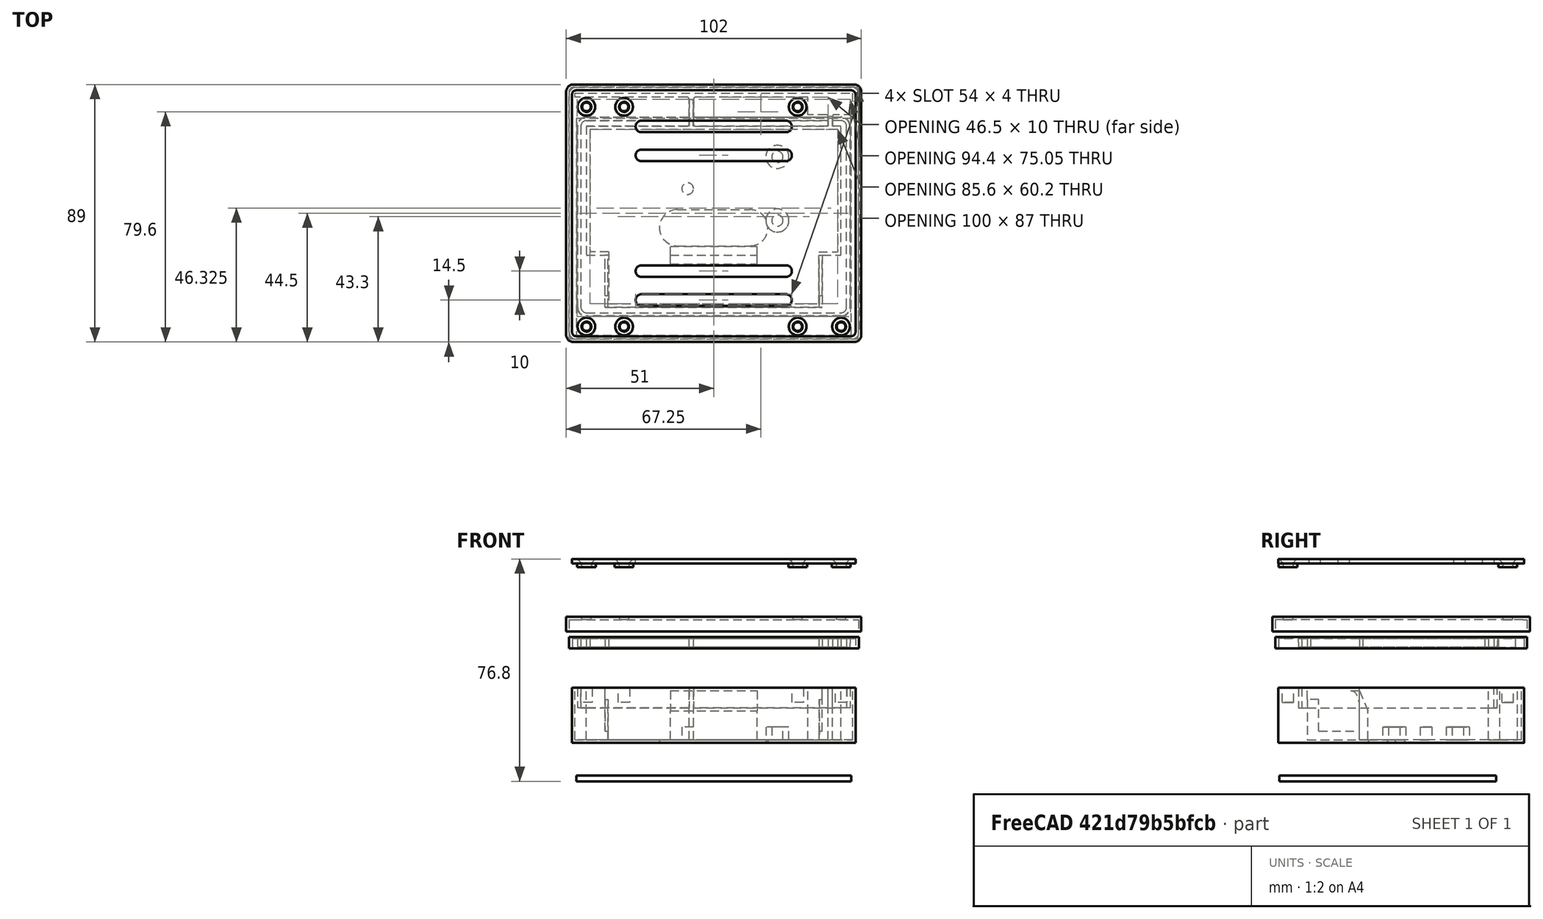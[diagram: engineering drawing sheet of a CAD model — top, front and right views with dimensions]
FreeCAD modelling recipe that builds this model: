
FCSTD DOCUMENT  (FreeCAD 1.1R20260325 (Git shallow))
Label: RAKTracker-v11.5
License: All rights reserved
objects: Sketcher::SketchObject×20, PartDesign::Pad×14, PartDesign::Body×5, App::Point×5, PartDesign::Pocket×4, PartDesign::SubShapeBinder×3, PartDesign::Plane×2, Spreadsheet::Sheet×1, PartDesign::AdditiveLoft×1, PartDesign::Hole×1
note: 110 computed .brp shape members not serialized (recipe doc carries the construction recipe); baked Part::Feature solids carry a one-line shape summary decoded from their .brp

FEATURE [Spreadsheet::Sheet] Spreadsheet  label="sheet"
  cells = A1='Components; D1='None-Component sizes; J1='TODO/NOTES; D3='M3 Insert Hole Dia; E3(InsetDiaM3)==3.9 mm; J3='We should really consider making the size of the panel the actual size and adjusting the boxantennaspace too.; A4='Solar Panel; D4='M2.5 Insert Hole DIa; E4(InsertDiaM2_5)==3.9 mm; J4='This means the panel needs to be aligned to one corner, and the antenna sizes need to create the width of the box.; A5='Panel width; B5(PanelWidth)==75 mm; D5='M3 Though Hall; E5(M3ThoughHoleDia)==3.2 mm; A6='Panel length; B6(PanelLength)==95 mm; D6='Insert Hole Depth; E6(InsertDepth)==8 mm; A7='Panel height; B7==1.5 mm; D8='PCB Mount Outer Diameter; E8(PCBMountDia)==8 mm; A9='Battery; D9='PCB Mount Height; E9(PCBMountHeight)==4.5 mm; A10='Battery Width; B10(BatteryWidth)==18 mm; D10='PCB Mount from Side; E10(PCBMountFromSide)==12 mm; A11='Battery Length; B11(BatteryLength)==65 mm; A12='Battery Height; B12(BatteryHeight)==18 mm; A13='Battery Mount Distance; B13(BatteryMountDistance)==75 mm; D14='Lid Wall Around sides; E14(LidWallAroundSides)==1 mm; A15='GPS Antenna Width; B15==15.5 mm; D15='Lid Wall Margin; E15==0.25 mm; A16='GPS Antenna Height; B16(AntGPSHeight)==7.5 mm; D16='Strap Mount Dia; E16(StrapMountDia)==8 mm; A17='GPS Antenna Length; B17(AntGPSLength)==15.5 mm; D17='Strap slot width; E17(StrapSlotWidth)==2 mm; D18='Strap slot distance; E18(StrapSlotDistance)==60 mm; A19='Small Molex Lora Antenna Width; B19(AntSmallLoraWidth)==10 mm; A20='Small Molex Lora Antenna Length; B20(AntSmallLoraLength)==80 mm; D20='SealWidth; E20(SealWidthTop)==1.2 mm; A21='Small Molex Lora Antenna Height; B21(AntSmallLoraHeight)==1.4 mm; D21='SealHeight; E21(SealHeight)==3 mm; D22='SealOuterWidth; E22(SealOuterWidth)==1 mm; A23='Large Molex Lora Antenna Width Sticker; B23(AntLargeLoraWidth)==12.5 mm; D23='Wall Width; E23(WallWidth)==5 mm; A24='Large Molex Lora Antenna Length Sticker; B24(AntLargeLoraLength)==87.5 mm; A25='Large Molex Lora Antenna Width (white); B25='TBD; A26='Large Molex Lora Antenna Length (white); B26==100 mm; D26='Bottom Thickness; E26(WallBottomThickness)==1 mm; A27='Large Molex Lora Antenna Height; B27(AntLargeLoraHeight)==1.6 mm; D27='Box Corner Radisu; E27(BoxCornerRadius)==1.5 mm; D28='BoxAntennaSpace; E28(BoxAntennaSpace)==10 mm; A29='Antenna Wire width; B29(AntWireWidth)==1.5 mm; A31='PCB Width; B31==30 mm; A32='PCB Length; B32==38 mm; A33='PCB Width With Margin; B33==31 mm; A34='PCB Length with Margin; B34==39 mm; A35='PCB Height; B35==16 mm; A36='PCB 2 Hole Distance; B36(PCBHoleDistance)==22 mm; A37='PCB Single Hole Distance from 2 Holes; B37(PCBHoleAwayFrom2Holes)==31 mm
FEATURE [Sketcher::SketchObject] Sketch  label="BoxBaseSketch"
  ArcFitTolerance = 1e-06
  AttachmentSupport = -> [XY_Plane]
  ExternalTypes = [0]
  FullyConstrained = true
  MakeInternals = false
  MapMode = 5
  _ExternalGeoVersion = 0
  expr: Constraints[18] = <<sheet>>.BoxCornerRadius
  expr: Constraints[28] = <<sheet>>.PanelLength
  expr: Constraints[29] = <<sheet>>.PanelWidth
  expr: Constraints[31] = <<sheet>>.BoxAntennaSpace
  expr: Constraints[40] = <<sheet>>.PanelWidth / 2
  sketch-geometry (18):
    g0: LineSegment StartX=-47.5 StartY=-42.5 StartZ=0 EndX=47.5 EndY=-42.5 EndZ=0
    g1: LineSegment StartX=49 StartY=-41 StartZ=0 EndX=49 EndY=41 EndZ=0
    g2: LineSegment StartX=47.5 StartY=42.5 StartZ=0 EndX=-47.5 EndY=42.5 EndZ=0
    g3: LineSegment StartX=-49 StartY=41 StartZ=0 EndX=-49 EndY=-41 EndZ=0
    g4: ArcOfCircle CenterX=-47.5 CenterY=-41 CenterZ=0 NormalX=0 NormalY=0 NormalZ=1 AngleXU=0 Radius=1.5 StartAngle=3.14159 EndAngle=4.71239
    g5: ArcOfCircle CenterX=47.5 CenterY=-41 CenterZ=0 NormalX=0 NormalY=0 NormalZ=1 AngleXU=0 Radius=1.5 StartAngle=4.71239 EndAngle=6.28319
    g6: ArcOfCircle CenterX=47.5 CenterY=41 CenterZ=0 NormalX=0 NormalY=0 NormalZ=1 AngleXU=0 Radius=1.5 StartAngle=-1.8e-15 EndAngle=1.5708
    g7: ArcOfCircle CenterX=-47.5 CenterY=41 CenterZ=0 NormalX=0 NormalY=0 NormalZ=1 AngleXU=0 Radius=1.5 StartAngle=1.5708 EndAngle=3.14159
    g8: GeomPoint [constr] X=49 Y=42.5 Z=0
    g9: GeomPoint [constr] X=0 Y=0 Z=0
    g10: LineSegment [constr] StartX=47.5 StartY=-42.5 StartZ=0 EndX=47.5 EndY=32.5 EndZ=0
    g11: LineSegment [constr] StartX=47.5 StartY=32.5 StartZ=0 EndX=-47.5 EndY=32.5 EndZ=0
    g12: LineSegment [constr] StartX=-47.5 StartY=32.5 StartZ=0 EndX=-47.5 EndY=-42.5 EndZ=0
    g13: LineSegment [constr] StartX=-47.5 StartY=-42.5 StartZ=0 EndX=47.5 EndY=-42.5 EndZ=0
    g14: ArcOfCircle CenterX=-12.5 CenterY=-5 CenterZ=0 NormalX=0 NormalY=0 NormalZ=1 AngleXU=0 Radius=6.25 StartAngle=1.5708 EndAngle=4.71239
    g15: ArcOfCircle CenterX=12.5 CenterY=-5 CenterZ=0 NormalX=0 NormalY=0 NormalZ=1 AngleXU=0 Radius=6.25 StartAngle=4.71239 EndAngle=7.85398
    g16: LineSegment StartX=-12.5 StartY=1.25 StartZ=0 EndX=12.5 EndY=1.25 EndZ=0
    g17: LineSegment StartX=-12.5 StartY=-11.25 StartZ=0 EndX=12.5 EndY=-11.25 EndZ=0
  constraints (41):
    c: Tangent(g0,g4) = -1.5708
    c: Tangent(g0,g5) = -1.5708
    c: Tangent(g1,g5) = -1.5708
    c: Tangent(g1,g6) = -1.5708
    c: Tangent(g2,g6) = -1.5708
    c: Tangent(g2,g7) = -1.5708
    c: Tangent(g3,g7) = -1.5708
    c: Tangent(g3,g4) = -1.5708
    c: Horizontal(g0)
    c: Horizontal(g2)
    c: Vertical(g1)
    c: Vertical(g3)
    c: Equal(g4,g5)
    c: Equal(g5,g6)
    c: Equal(g6,g7)
    c: Symmetric(g2,g0,g9)
    c: PointOnObject(g8,g1)
    c: PointOnObject(g8,g2)
    c: Radius(g5) = 1.5
    c: Coincident(g9,g-1)
    c: Coincident(g10,g11)
    c: Coincident(g11,g12)
    c: Coincident(g12,g13)
    c: Coincident(g13,g10)
    c: Vertical(g10)
    c: Vertical(g12)
    c: Horizontal(g11)
    c: Coincident(g10,g0)
    c: DistanceX(g12,g0) = 95
    c: DistanceY(g10,g10) = 75
    c: Coincident(g12,g0)
    c: DistanceY(g10,g2) = 10
    c: Tangent(g14,g16) = 1.5708
    c: Tangent(g14,g17) = -1.5708
    c: Tangent(g15,g16) = 1.5708
    c: Tangent(g15,g17) = -1.5708
    c: Equal(g14,g15)
    c: Distance(g15,g15) = 12.5
    c: DistanceX(g14,g15) = 25
    c: Symmetric(g14,g15,g-2)
    c: DistanceY(g15,g10) = 37.5
FEATURE [PartDesign::Pad] Pad  label="BoxBase"
  Direction = (0,0,1)
  Length = 1
  Length2 = 10
  Profile = -> Sketch
  ReferenceAxis = -> Sketch [N_Axis]
  SideType = 0
  Suppressed = false
  Type = 0
  Type2 = 0
  expr: Length = <<sheet>>.WallBottomThickness
FEATURE [Sketcher::SketchObject] Sketch001  label="BoxOuterWallSketch"
  ArcFitTolerance = 1e-06
  AttachmentSupport = -> [XY_Plane]
  ExternalTypes = [0]
  FullyConstrained = true
  MakeInternals = false
  MapMode = 5
  _ExternalGeoVersion = 0
  expr: Constraints[100] = <<sheet>>.PanelWidth
  expr: Constraints[101] = <<sheet>>.PanelLength
  expr: Constraints[103] = <<sheet>>.BoxAntennaSpace
  expr: Constraints[115] = <<sheet>>.BoxCornerRadius
  expr: Constraints[129] = <<sheet>>.WallWidth
  expr: Constraints[49] = <<sheet>>.AntGPSLength
  expr: Constraints[50] = <<sheet>>.AntWireWidth
  expr: Constraints[51] = <<sheet>>.BatteryMountDistance
  expr: Constraints[52] = <<sheet>>.WallWidth * 2
  expr: Constraints[53] = <<sheet>>.WallWidth
  expr: Constraints[54] = <<sheet>>.BatteryWidth
  expr: Constraints[87] = <<sheet>>.AntWireWidth
  expr: Constraints[90] = <<sheet>>.AntSmallLoraHeight
  expr: Constraints[91] = <<sheet>>.AntGPSHeight
  expr: Constraints[92] = <<sheet>>.WallWidth * 2
  sketch-geometry (48):
    g0: LineSegment StartX=-47.5 StartY=-42.5 StartZ=0 EndX=47.5 EndY=-42.5 EndZ=0
    g1: LineSegment StartX=49 StartY=-41 StartZ=0 EndX=49 EndY=41 EndZ=0
    g2: LineSegment StartX=47.5 StartY=42.5 StartZ=0 EndX=-47.5 EndY=42.5 EndZ=0
    g3: LineSegment StartX=44 StartY=30.1 StartZ=0 EndX=44 EndY=-14.5 EndZ=0
    g4: LineSegment StartX=44 StartY=-14.5 StartZ=0 EndX=37.5 EndY=-14.5 EndZ=0
    g5: LineSegment StartX=37.5 StartY=-14.5 StartZ=0 EndX=37.5 EndY=-32.5 EndZ=0
    g6: LineSegment StartX=37.5 StartY=-32.5 StartZ=0 EndX=-37.5 EndY=-32.5 EndZ=0
    g7: LineSegment StartX=-37.5 StartY=-32.5 StartZ=0 EndX=-37.5 EndY=-14.5 EndZ=0
    g8: LineSegment StartX=-37.5 StartY=-14.5 StartZ=0 EndX=-44 EndY=-14.5 EndZ=0
    g9: LineSegment StartX=-44 StartY=-14.5 StartZ=0 EndX=-44 EndY=30.1 EndZ=0
    g10: LineSegment StartX=-44 StartY=30.1 StartZ=0 EndX=-9.25 EndY=30.1 EndZ=0
    g11: LineSegment StartX=-8.5 StartY=30.85 StartZ=0 EndX=-8.5 EndY=39.35 EndZ=0
    g12: LineSegment StartX=-9.25 StartY=40.1 StartZ=0 EndX=-48 EndY=40.1 EndZ=0
    g13: LineSegment StartX=-48 StartY=40.1 StartZ=0 EndX=-48 EndY=41.5 EndZ=0
    g14: LineSegment StartX=-48 StartY=41.5 StartZ=0 EndX=48 EndY=41.5 EndZ=0
    g15: LineSegment StartX=-7 StartY=30.85 StartZ=0 EndX=-7 EndY=39.35 EndZ=0
    g16: LineSegment StartX=-6.25 StartY=40.1 StartZ=0 EndX=32.5 EndY=40.1 EndZ=0
    g17: LineSegment StartX=32.5 StartY=40.1 StartZ=0 EndX=32.5 EndY=34 EndZ=0
    g18: LineSegment StartX=48 StartY=34 StartZ=0 EndX=48 EndY=41.5 EndZ=0
    g19: ArcOfCircle CenterX=-9.25 CenterY=39.35 CenterZ=0 NormalX=0 NormalY=0 NormalZ=1 AngleXU=0 Radius=0.75 StartAngle=3e-15 EndAngle=1.5708
    g20: GeomPoint [constr] X=-8.5 Y=40.1 Z=0
    g21: ArcOfCircle CenterX=-6.25 CenterY=39.35 CenterZ=0 NormalX=0 NormalY=0 NormalZ=1 AngleXU=0 Radius=0.75 StartAngle=1.5708 EndAngle=3.14159
    g22: ArcOfCircle CenterX=-9.25 CenterY=30.85 CenterZ=0 NormalX=0 NormalY=0 NormalZ=1 AngleXU=0 Radius=0.75 StartAngle=4.71239 EndAngle=6.28319
    g23: GeomPoint [constr] X=-8.5 Y=30.1 Z=0
    g24: ArcOfCircle CenterX=-6.25 CenterY=30.85 CenterZ=0 NormalX=0 NormalY=0 NormalZ=1 AngleXU=0 Radius=0.75 StartAngle=3.14159 EndAngle=4.71239
    g25: LineSegment StartX=32.5 StartY=34 StartZ=0 EndX=39 EndY=34 EndZ=0
    g26: LineSegment StartX=39.5 StartY=33.5 StartZ=0 EndX=39.5 EndY=30.6 EndZ=0
    g27: LineSegment StartX=39 StartY=30.1 StartZ=0 EndX=-6.25 EndY=30.1 EndZ=0
    g28: LineSegment StartX=48 StartY=34 StartZ=0 EndX=41.5 EndY=34 EndZ=0
    g29: LineSegment StartX=41 StartY=33.5 StartZ=0 EndX=41 EndY=30.6 EndZ=0
    g30: LineSegment StartX=41.5 StartY=30.1 StartZ=0 EndX=44 EndY=30.1 EndZ=0
    g31: ArcOfCircle CenterX=39 CenterY=33.5 CenterZ=0 NormalX=0 NormalY=0 NormalZ=1 AngleXU=0 Radius=0.5 StartAngle=0 EndAngle=1.5708
    g32: GeomPoint [constr] X=39.5 Y=34 Z=0
    g33: ArcOfCircle CenterX=41.5 CenterY=33.5 CenterZ=0 NormalX=0 NormalY=0 NormalZ=1 AngleXU=0 Radius=0.5 StartAngle=1.5708 EndAngle=3.14159
    g34: GeomPoint [constr] X=41 Y=34 Z=0
    g35: ArcOfCircle CenterX=39 CenterY=30.6 CenterZ=0 NormalX=0 NormalY=0 NormalZ=1 AngleXU=0 Radius=0.5 StartAngle=4.71239 EndAngle=6.28319
    g36: GeomPoint [constr] X=39.5 Y=30.1 Z=0
    g37: ArcOfCircle CenterX=41.5 CenterY=30.6 CenterZ=0 NormalX=0 NormalY=0 NormalZ=1 AngleXU=0 Radius=0.5 StartAngle=3.14159 EndAngle=4.71239
    g38: GeomPoint [constr] X=41 Y=30.1 Z=0
    g39: LineSegment [constr] StartX=-47.5 StartY=32.5 StartZ=0 EndX=-47.5 EndY=-42.5 EndZ=0
    g40: LineSegment [constr] StartX=-47.5 StartY=-42.5 StartZ=0 EndX=47.5 EndY=-42.5 EndZ=0
    g41: LineSegment [constr] StartX=47.5 StartY=-42.5 StartZ=0 EndX=47.5 EndY=32.5 EndZ=0
    g42: LineSegment [constr] StartX=47.5 StartY=32.5 StartZ=0 EndX=-47.5 EndY=32.5 EndZ=0
    g43: LineSegment StartX=-49 StartY=41 StartZ=0 EndX=-49 EndY=-41 EndZ=0
    g44: ArcOfCircle CenterX=-47.5 CenterY=-41 CenterZ=0 NormalX=0 NormalY=0 NormalZ=1 AngleXU=0 Radius=1.5 StartAngle=3.14159 EndAngle=4.71239
    g45: ArcOfCircle CenterX=47.5 CenterY=-41 CenterZ=0 NormalX=0 NormalY=0 NormalZ=1 AngleXU=0 Radius=1.5 StartAngle=4.71239 EndAngle=6.28319
    g46: ArcOfCircle CenterX=47.5 CenterY=41 CenterZ=0 NormalX=0 NormalY=0 NormalZ=1 AngleXU=0 Radius=1.5 StartAngle=0 EndAngle=1.5708
    g47: ArcOfCircle CenterX=-47.5 CenterY=41 CenterZ=0 NormalX=0 NormalY=0 NormalZ=1 AngleXU=0 Radius=1.5 StartAngle=1.5708 EndAngle=3.14159
  constraints (132):
    c: Vertical(g1)
    c: Horizontal(g2)
    c: Vertical(g3)
    c: Coincident(g3,g4)
    c: Horizontal(g4)
    c: Coincident(g4,g5)
    c: Vertical(g5)
    c: Coincident(g5,g6)
    c: Horizontal(g6)
    c: Coincident(g6,g7)
    c: Vertical(g7)
    c: Coincident(g7,g8)
    c: Coincident(g8,g9)
    c: Vertical(g9)
    c: Coincident(g9,g10)
    c: Horizontal(g10)
    c: Coincident(g12,g13)
    c: Coincident(g13,g14)
    c: Horizontal(g14)
    c: Horizontal(g8)
    c: Vertical(g15)
    c: Horizontal(g16)
    c: Coincident(g16,g17)
    c: Coincident(g18,g14)
    c: Vertical(g18)
    c: Vertical(g17)
    c: Vertical(g11)
    c: Vertical(g13)
    c: Horizontal(g12)
    c: PointOnObject(g20,g12)
    c: PointOnObject(g20,g11)
    c: Tangent(g12,g19) = -1.5708
    c: Tangent(g11,g19) = -1.5708
    c: Tangent(g15,g21) = 1.5708
    c: Tangent(g16,g21) = 1.5708
    c: PointOnObject(g23,g11)
    c: PointOnObject(g23,g10)
    c: Tangent(g11,g22) = -1.5708
    c: Tangent(g10,g22) = -1.5708
    c: Tangent(g15,g24) = 1.5708
    c: Radius(g19) = 0.75
    c: Equal(g19,g22)
    c: Equal(g22,g21)
    c: Equal(g21,g24)
    c: Horizontal(g11,g15)
    c: Horizontal(g7,g4)
    c: Equal(g8,g4)
    c: DistanceY(g13,g2) = 1
    c: DistanceX(g14,g1) = 1
    c: DistanceX(g17,g18) = 15.5
    c: DistanceX(g11,g15) = 1.5
    c: DistanceX(g7,g4) = 75
    c: DistanceY(g0,g6) = 10
    c: DistanceX(g3,g1) = 5
    c: DistanceY(g5,g4) = 18
    c: Coincident(g17,g25)
    c: Coincident(g27,g24)
    c: Horizontal(g27)
    c: Coincident(g18,g28)
    c: Horizontal(g28)
    c: Coincident(g30,g3)
    c: Horizontal(g25)
    c: Vertical(g29)
    c: Vertical(g26)
    c: Horizontal(g30)
    c: PointOnObject(g32,g25)
    c: PointOnObject(g32,g26)
    c: Tangent(g25,g31) = 1.5708
    c: Tangent(g26,g31) = 1.5708
    c: PointOnObject(g34,g29)
    c: PointOnObject(g34,g28)
    c: Tangent(g29,g33) = -1.5708
    c: Tangent(g28,g33) = -1.5708
    c: PointOnObject(g36,g26)
    c: PointOnObject(g36,g27)
    c: Tangent(g26,g35) = 1.5708
    c: Tangent(g27,g35) = 1.5708
    c: PointOnObject(g38,g30)
    c: PointOnObject(g38,g29)
    c: Tangent(g30,g37) = -1.5708
    c: Tangent(g29,g37) = -1.5708
    c: Radius(g31) = 0.5
    c: Equal(g31,g33)
    c: Equal(g33,g35)
    c: Equal(g35,g37)
    c: Horizontal(g30,g27)
    c: Horizontal(g25,g28)
    c: DistanceX(g26,g29) = 1.5
    c: Equal(g25,g28)
    c: Horizontal(g10,g24)
    c: DistanceY(g12,g13) = 1.4
    c: DistanceY(g18,g14) = 7.5
    c: DistanceY(g9,g12) = 10
    c: Coincident(g39,g40)
    c: Coincident(g41,g42)
    c: Coincident(g42,g39)
    c: Vertical(g39)
    c: Vertical(g41)
    c: Horizontal(g42)
    c: Horizontal(g0)
    c: DistanceY(g39,g39) = 75
    c: DistanceX(g40,g40) = 95
    c: Coincident(g41,g40)
    c: DistanceY(g41,g2) = 10
    c: Coincident(g0,g39)
    c: Coincident(g0,g40)
    c: Vertical(g43)
    c: Coincident(g44,g0)
    c: Coincident(g44,g43)
    c: Coincident(g45,g0)
    c: Coincident(g45,g1)
    c: Coincident(g46,g2)
    c: Coincident(g46,g1)
    c: Coincident(g47,g43)
    c: Coincident(g47,g2)
    c: Radius(g47) = 1.5
    c: Horizontal(g47,g43)
    c: Vertical(g47,g2)
    c: Equal(g47,g46)
    c: Vertical(g2,g46)
    c: Horizontal(g1,g46)
    c: Vertical(g44,g0)
    c: Horizontal(g43,g44)
    c: Horizontal(g1,g45)
    c: Vertical(g0,g45)
    c: DistanceX(g43,g12) = 1
    c: Symmetric(g2,g0,g-1)
    c: Vertical(g39,g47)
    c: Vertical(g41,g46)
    c: DistanceX(g43,g8) = 5
    c: DistanceX(g12,g11) = 39.5
    c: Horizontal(g12,g16)
FEATURE [PartDesign::Pad] Pad001  label="BoxWall"
  BaseFeature = -> Pad
  Direction = (0,0,1)
  Length = 19
  Length2 = 10
  Profile = -> Sketch001
  ReferenceAxis = -> Sketch001 [N_Axis]
  SideType = 0
  Suppressed = false
  Type = 0
  Type2 = 0
  expr: Length = <<sheet>>.BatteryWidth + <<sheet>>.WallBottomThickness
FEATURE [Sketcher::SketchObject] Sketch002  label="BoxPCBMountSketch"
  ArcFitTolerance = 1e-06
  AttachmentSupport = -> [XY_Plane]
  ExternalGeometry = -> [Sketch001]
  ExternalTypes = [0]
  FullyConstrained = true
  MakeInternals = false
  MapMode = 5
  _ExternalGeoVersion = 0
  expr: Constraints[10] = <<sheet>>.PCBMountFromSide
  expr: Constraints[11] = <<sheet>>.PCBHoleAwayFrom2Holes
  expr: Constraints[2] = <<sheet>>.InsetDiaM3
  expr: Constraints[5] = <<sheet>>.PCBMountDia
  expr: Constraints[7] = <<sheet>>.PCBHoleDistance
  expr: Constraints[8] = <<sheet>>.PCBMountDia / 2
  expr: Constraints[9] = <<sheet>>.PCBHoleDistance / 2
  sketch-geometry (5):
    g0: Circle CenterX=22 CenterY=19.5 CenterZ=0 NormalX=0 NormalY=0 NormalZ=1 AngleXU=0 Radius=4
    g1: Circle CenterX=22 CenterY=-2.5 CenterZ=0 NormalX=0 NormalY=0 NormalZ=1 AngleXU=0 Radius=4
    g2: Circle CenterX=22 CenterY=-2.5 CenterZ=0 NormalX=0 NormalY=0 NormalZ=1 AngleXU=0 Radius=1.95
    g3: Circle CenterX=22 CenterY=19.5 CenterZ=0 NormalX=0 NormalY=0 NormalZ=1 AngleXU=0 Radius=1.95
    g4: Circle CenterX=-9 CenterY=8.5 CenterZ=0 NormalX=0 NormalY=0 NormalZ=1 AngleXU=0 Radius=2
  constraints (13):
    c: Coincident(g2,g1)
    c: Coincident(g3,g0)
    c: Diameter(g3) = 3.9
    c: Equal(g3,g2)
    c: Vertical(g1,g0)
    c: Diameter(g0) = 8
    c: Equal(g0,g1)
    c: DistanceY(g1,g0) = 22
    c: Diameter(g4) = 4
    c: DistanceY(g1,g4) = 11
    c: DistanceY(g-3,g1) = 12
    c: DistanceX(g4,g0) = 31
    c: DistanceX(g1,g-3) = 22
FEATURE [PartDesign::Pad] Pad002  label="BoxPCBMount"
  BaseFeature = -> Pad001
  Direction = (0,0,1)
  Length = 5.5
  Length2 = 10
  Profile = -> Sketch002
  ReferenceAxis = -> Sketch002 [N_Axis]
  SideType = 0
  Suppressed = false
  Type = 0
  Type2 = 0
  expr: Length = <<sheet>>.WallBottomThickness + <<sheet>>.PCBMountHeight
FEATURE [Sketcher::SketchObject] Sketch003  label="BoxBatteryHolderSketch"
  ArcFitTolerance = 1e-06
  AttachmentSupport = -> [YZ_Plane]
  ExternalGeometry = -> [Sketch001]
  ExternalTypes = [0]
  FullyConstrained = true
  MakeInternals = false
  MapMode = 5
  Placement = pos=(0,0,0) rot=(0.57735,0.57735,0.57735;2.0944rad)
  _ExternalGeoVersion = 0
  expr: Constraints[21] = <<sheet>>.BatteryWidth
  sketch-geometry (11):
    g0: LineSegment StartX=-14.5 StartY=0 StartZ=0 EndX=-14.5 EndY=11 EndZ=0
    g1: LineSegment StartX=-14.5 StartY=0 StartZ=0 EndX=-11.5 EndY=0 EndZ=0
    g2: LineSegment StartX=-11.5 StartY=0 StartZ=0 EndX=-11.5 EndY=11 EndZ=0
    g3: Circle [constr] CenterX=-17.5 CenterY=18 CenterZ=0 NormalX=0 NormalY=0 NormalZ=1 AngleXU=0 Radius=1
    g4: Circle [constr] CenterX=-14.5 CenterY=18 CenterZ=0 NormalX=0 NormalY=0 NormalZ=1 AngleXU=0 Radius=1
    g5: Circle [constr] CenterX=-14.5 CenterY=11 CenterZ=0 NormalX=0 NormalY=0 NormalZ=1 AngleXU=0 Radius=1
    g6: BSplineCurve PolesCount=3 KnotsCount=2 Degree=2 IsPeriodic=0
    g7: GeomPoint [constr] X=-17.5 Y=18 Z=0
    g8: GeomPoint [constr] X=-14.5 Y=11 Z=0
    g9: LineSegment StartX=-17.5 StartY=18 StartZ=0 EndX=-14.5 EndY=18 EndZ=0
    g10: LineSegment StartX=-14.5 StartY=18 StartZ=0 EndX=-11.5 EndY=11 EndZ=0
  constraints (26):
    c: Coincident(g0,g-3)
    c: Vertical(g0)
    c: Coincident(g1,g0)
    c: PointOnObject(g1,g-1)
    c: Coincident(g2,g1)
    c: Vertical(g2)
    c: Weight(g3) = 1
    c: Equal(g3,g4)
    c: Equal(g3,g5)
    c: InternalAlignment(g3,g6)
    c: InternalAlignment(g4,g6)
    c: InternalAlignment(g5,g6)
    c: InternalAlignment(g7,g6)
    c: InternalAlignment(g8,g6)
    c: Coincident(g6,g0)
    c: DistanceX(g1,g1) = 3
    c: DistanceY(g0,g0) = 11
    c: Coincident(g9,g6)
    c: Horizontal(g9)
    c: Coincident(g10,g9)
    c: Coincident(g10,g2)
    c: DistanceY(g1,g9) = 18
    c: Horizontal(g0,g2)
    c: DistanceX(g6,g9) = 3
    c: Vertical(g0,g9)
    c: Coincident(g4,g9)
FEATURE [PartDesign::Pad] Pad003  label="BoxBatteryHolder"
  BaseFeature = -> Pad002
  Direction = (1,0,0)
  Length = 30
  Length2 = 10
  Profile = -> Sketch003
  ReferenceAxis = -> Sketch003 [N_Axis]
  SideType = 2
  Suppressed = false
  Type = 0
  Type2 = 0
FEATURE [Sketcher::SketchObject] Sketch004  label="BoxSealPocketSketch"
  ArcFitTolerance = 1e-06
  AttachmentSupport = -> [Pad003]
  ExternalGeometry = -> [Sketch001]
  ExternalTypes = [0]
  FullyConstrained = true
  MakeInternals = false
  MapMode = 5
  Placement = pos=(0,0,19) rot=(0,0,1;0rad)
  _ExternalGeoVersion = 0
  expr: Constraints[33] = <<sheet>>.SealWidthTop
  expr: Constraints[34] = (<<sheet>>.WallWidth - <<sheet>>.SealWidthTop) / 2
  expr: Constraints[35] = (<<sheet>>.WallWidth - <<sheet>>.SealWidthTop) / 2
  expr: Constraints[38] = (<<sheet>>.WallWidth - <<sheet>>.SealWidthTop) / 2
  sketch-geometry (18):
    g0: LineSegment StartX=47.1 StartY=-32.5 StartZ=0 EndX=47.1 EndY=30.1 EndZ=0
    g1: LineSegment StartX=44 StartY=33.2 StartZ=0 EndX=-44 EndY=33.2 EndZ=0
    g2: LineSegment StartX=-47.1 StartY=30.1 StartZ=0 EndX=-47.1 EndY=-32.5 EndZ=0
    g3: LineSegment StartX=-44 StartY=-35.6 StartZ=0 EndX=44 EndY=-35.6 EndZ=0
    g4: ArcOfCircle CenterX=44 CenterY=-32.5 CenterZ=0 NormalX=0 NormalY=0 NormalZ=1 AngleXU=0 Radius=3.1 StartAngle=4.71239 EndAngle=6.28319
    g5: ArcOfCircle CenterX=44 CenterY=30.1 CenterZ=0 NormalX=0 NormalY=0 NormalZ=1 AngleXU=0 Radius=3.1 StartAngle=-5.33e-14 EndAngle=1.5708
    g6: ArcOfCircle CenterX=-44 CenterY=30.1 CenterZ=0 NormalX=0 NormalY=0 NormalZ=1 AngleXU=0 Radius=3.1 StartAngle=1.5708 EndAngle=3.14159
    g7: ArcOfCircle CenterX=-44 CenterY=-32.5 CenterZ=0 NormalX=0 NormalY=0 NormalZ=1 AngleXU=0 Radius=3.1 StartAngle=3.14159 EndAngle=4.71239
    g8: LineSegment StartX=45.9 StartY=-32.5 StartZ=0 EndX=45.9 EndY=30.1 EndZ=0
    g9: LineSegment StartX=44 StartY=32 StartZ=0 EndX=-44 EndY=32 EndZ=0
    g10: LineSegment StartX=-45.9 StartY=30.1 StartZ=0 EndX=-45.9 EndY=-32.5 EndZ=0
    g11: LineSegment StartX=-44 StartY=-34.4 StartZ=0 EndX=44 EndY=-34.4 EndZ=0
    g12: ArcOfCircle CenterX=44 CenterY=-32.5 CenterZ=0 NormalX=0 NormalY=0 NormalZ=1 AngleXU=0 Radius=1.9 StartAngle=4.71239 EndAngle=6.28319
    g13: ArcOfCircle CenterX=44 CenterY=30.1 CenterZ=0 NormalX=0 NormalY=0 NormalZ=1 AngleXU=0 Radius=1.9 StartAngle=4.234e-13 EndAngle=1.5708
    g14: ArcOfCircle CenterX=-44 CenterY=30.1 CenterZ=0 NormalX=0 NormalY=0 NormalZ=1 AngleXU=0 Radius=1.9 StartAngle=1.5708 EndAngle=3.14159
    g15: ArcOfCircle CenterX=-44 CenterY=-32.5 CenterZ=0 NormalX=0 NormalY=0 NormalZ=1 AngleXU=0 Radius=1.9 StartAngle=3.14159 EndAngle=4.71239
    g16: GeomPoint [constr] X=-47.1 Y=33.2 Z=0
    g17: GeomPoint [constr] X=0 Y=0 Z=0
  constraints (39):
    c: Tangent(g0,g4) = -1.5708
    c: Tangent(g0,g5) = -1.5708
    c: Tangent(g1,g5) = -1.5708
    c: Tangent(g1,g6) = -1.5708
    c: Tangent(g2,g6) = -1.5708
    c: Tangent(g2,g7) = -1.5708
    c: Tangent(g3,g7) = -1.5708
    c: Tangent(g3,g4) = -1.5708
    c: Vertical(g0)
    c: Vertical(g2)
    c: Horizontal(g1)
    c: Horizontal(g3)
    c: Equal(g4,g5)
    c: Equal(g5,g6)
    c: Equal(g6,g7)
    c: Tangent(g8,g12) = -1.5708
    c: Tangent(g8,g13) = -1.5708
    c: Tangent(g9,g13) = -1.5708
    c: Tangent(g9,g14) = -1.5708
    c: Tangent(g10,g14) = -1.5708
    c: Tangent(g10,g15) = -1.5708
    c: Tangent(g11,g15) = -1.5708
    c: Tangent(g11,g12) = -1.5708
    c: Coincident(g4,g12)
    c: Coincident(g5,g13)
    c: Coincident(g6,g14)
    c: Coincident(g7,g15)
    c: Vertical(g8)
    c: Vertical(g10)
    c: Horizontal(g9)
    c: PointOnObject(g16,g1)
    c: PointOnObject(g16,g2)
    c: Coincident(g17,g-1)
    c: DistanceY(g9,g1) = 1.2
    c: DistanceY(g11,g-4) = 1.9
    c: DistanceY(g-3,g9) = 1.9
    c: Vertical(g-3,g9)
    c: Horizontal(g10,g-3)
    c: DistanceX(g-5,g8) = 1.9
FEATURE [PartDesign::Pocket] Pocket  label="BoxSealPocket"
  BaseFeature = -> Pad003
  Direction = (0,0,-1)
  Length = 7
  Length2 = 5
  Profile = -> Sketch004
  ReferenceAxis = -> Sketch004 [N_Axis]
  SideType = 0
  Suppressed = false
  Type = 0
  Type2 = 0
FEATURE [Sketcher::SketchObject] Sketch005  label="BoxBatteryClip1Sketch"
  ArcFitTolerance = 1e-06
  AttachmentOffset = pos=(0,0,36.5) rot=(0,0,1;0rad)
  AttachmentSupport = -> [YZ_Plane]
  ExternalGeometry = -> [Sketch001]
  ExternalTypes = [0]
  FullyConstrained = true
  MakeInternals = false
  MapMode = 5
  Placement = pos=(36.5,0,0) rot=(0.57735,0.57735,0.57735;2.0944rad)
  _ExternalGeoVersion = 0
  expr: .AttachmentOffset.Base.z = <<sheet>>.BatteryMountDistance / 2 - 1 mm
  expr: Constraints[15] = <<sheet>>.BatteryWidth - <<sheet>>.SealHeight
  sketch-geometry (6):
    g0: LineSegment StartX=-14.5 StartY=0 StartZ=0 EndX=-14.5 EndY=4 EndZ=0
    g1: LineSegment StartX=-28.5 StartY=4 StartZ=0 EndX=-14.5 EndY=4 EndZ=0
    g2: LineSegment StartX=-28.5 StartY=4 StartZ=0 EndX=-28.5 EndY=15 EndZ=0
    g3: LineSegment StartX=-28.5 StartY=15 StartZ=0 EndX=-32.5 EndY=15 EndZ=0
    g4: LineSegment StartX=-32.5 StartY=15 StartZ=0 EndX=-32.5 EndY=0 EndZ=0
    g5: LineSegment StartX=-32.5 StartY=0 StartZ=0 EndX=-14.5 EndY=0 EndZ=0
  constraints (16):
    c: Coincident(g-3,g0)
    c: Vertical(g0)
    c: Coincident(g1,g0)
    c: Horizontal(g1)
    c: Coincident(g1,g2)
    c: Vertical(g2)
    c: Coincident(g2,g3)
    c: Horizontal(g3)
    c: Coincident(g3,g4)
    c: Coincident(g4,g-3)
    c: Coincident(g4,g5)
    c: Coincident(g5,g0)
    c: Vertical(g4)
    c: DistanceX(g3,g3) = 4
    c: DistanceY(g0,g0) = 4
    c: DistanceY(g4,g3) = 15
FEATURE [PartDesign::Pad] Pad004  label="BoxBatteryClip1"
  BaseFeature = -> Pocket
  Direction = (1,0,0)
  Length = 1
  Length2 = 10
  Profile = -> Sketch005
  ReferenceAxis = -> Sketch005 [N_Axis]
  SideType = 0
  Suppressed = false
  Type = 0
  Type2 = 0
FEATURE [Sketcher::SketchObject] Sketch006  label="BoxBatteryClip2Sketch"
  ArcFitTolerance = 1e-06
  AttachmentOffset = pos=(0,0,-37.5) rot=(0,0,1;0rad)
  AttachmentSupport = -> [YZ_Plane]
  ExternalGeometry = -> [Sketch001]
  ExternalTypes = [0]
  FullyConstrained = true
  MakeInternals = false
  MapMode = 5
  Placement = pos=(-37.5,0,0) rot=(0.57735,0.57735,0.57735;2.0944rad)
  _ExternalGeoVersion = 0
  expr: .AttachmentOffset.Base.z = <<sheet>>.BatteryMountDistance / 2 mm * -1 mm
  expr: Constraints[14] = <<sheet>>.BatteryWidth - <<sheet>>.SealHeight
  sketch-geometry (6):
    g0: LineSegment StartX=-32.5 StartY=0 StartZ=0 EndX=-32.5 EndY=15 EndZ=0
    g1: LineSegment StartX=-32.5 StartY=15 StartZ=0 EndX=-28.5 EndY=15 EndZ=0
    g2: LineSegment StartX=-28.5 StartY=15 StartZ=0 EndX=-28.5 EndY=4 EndZ=0
    g3: LineSegment StartX=-28.5 StartY=4 StartZ=0 EndX=-14.5 EndY=4 EndZ=0
    g4: LineSegment StartX=-14.5 StartY=4 StartZ=0 EndX=-14.5 EndY=0 EndZ=0
    g5: LineSegment StartX=-14.5 StartY=0 StartZ=0 EndX=-32.5 EndY=0 EndZ=0
  constraints (16):
    c: Coincident(g-3,g0)
    c: Vertical(g0)
    c: Coincident(g0,g1)
    c: Coincident(g1,g2)
    c: Coincident(g2,g3)
    c: Coincident(g3,g4)
    c: Coincident(g4,g-3)
    c: Coincident(g4,g5)
    c: Coincident(g5,g0)
    c: Horizontal(g3)
    c: Vertical(g4)
    c: Vertical(g2)
    c: Horizontal(g1)
    c: DistanceY(g4,g4) = 4
    c: DistanceY(g0,g0) = 15
    c: DistanceX(g0,g1) = 4
FEATURE [PartDesign::Plane] DatumPlane  label="BoxTop"
  Length = 116.254
  MapMode = 5
  Placement = pos=(0,0,19) rot=(0,0,1;0rad)
  ResizeMode = 0
  Width = 103.254
FEATURE [Sketcher::SketchObject] Sketch007  label="BoxLidHolesSketch"
  ArcFitTolerance = 1e-06
  AttachmentSupport = -> [DatumPlane]
  ExternalGeometry = -> [Sketch001]
  ExternalTypes = [0]
  FullyConstrained = true
  MakeInternals = false
  MapMode = 5
  Placement = pos=(0,0,19) rot=(0,0,1;0rad)
  _ExternalGeoVersion = 0
  expr: Constraints[15] = <<sheet>>.WallWidth / 3 * 2
  expr: Constraints[16] = <<sheet>>.WallWidth / 3 * 2
  expr: Constraints[17] = <<sheet>>.WallWidth
  expr: Constraints[18] = <<sheet>>.WallWidth
  expr: Constraints[8] = <<sheet>>.InsetDiaM3
  sketch-geometry (7):
    g0: Circle CenterX=-44 CenterY=-39.1667 CenterZ=0 NormalX=0 NormalY=0 NormalZ=1 AngleXU=0 Radius=1.95
    g1: Circle CenterX=44 CenterY=-39.1667 CenterZ=0 NormalX=0 NormalY=0 NormalZ=1 AngleXU=0 Radius=1.95
    g2: Circle CenterX=-44 CenterY=36.7667 CenterZ=0 NormalX=0 NormalY=0 NormalZ=1 AngleXU=0 Radius=1.95
    g3: Circle CenterX=29 CenterY=36.7667 CenterZ=0 NormalX=0 NormalY=0 NormalZ=1 AngleXU=0 Radius=1.95
    g4: Circle CenterX=-31 CenterY=36.7667 CenterZ=0 NormalX=0 NormalY=0 NormalZ=1 AngleXU=0 Radius=1.95
    g5: Circle CenterX=29 CenterY=-39.1667 CenterZ=0 NormalX=0 NormalY=0 NormalZ=1 AngleXU=0 Radius=1.95
    g6: Circle CenterX=-31 CenterY=-39.1667 CenterZ=0 NormalX=0 NormalY=0 NormalZ=1 AngleXU=0 Radius=1.95
  constraints (21):
    c: Horizontal(g6,g5)
    c: Horizontal(g5,g1)
    c: Horizontal(g1,g0)
    c: DistanceX(g6,g5) = 60
    c: Vertical(g6,g4)
    c: Vertical(g3,g5)
    c: Vertical(g0,g2)
    c: Horizontal(g2,g4)
    c: Diameter(g0) = 3.9
    c: Equal(g0,g1)
    c: Equal(g1,g2)
    c: Equal(g2,g3)
    c: Equal(g3,g4)
    c: Equal(g4,g5)
    c: Equal(g5,g6)
    c: DistanceY(g-3,g0) = 3.33333
    c: DistanceY(g2,g-4) = 3.33333
    c: DistanceX(g1,g-6) = 5
    c: DistanceX(g-5,g0) = 5
    c: Horizontal(g4,g3)
    c: Distance(g4,g-2) = 31
FEATURE [PartDesign::Pocket] Pocket001  label="BoxLidHoles"
  BaseFeature = -> Pad004
  Direction = (0,0,-1)
  Length = 5
  Length2 = 5
  Profile = -> Sketch007
  ReferenceAxis = -> Sketch007 [N_Axis]
  SideType = 0
  Suppressed = false
  Type = 0
  Type2 = 0
FEATURE [Sketcher::SketchObject] Sketch008  label="SealBaseSketch"
  ArcFitTolerance = 1e-06
  AttachmentSupport = -> [XY_Plane001]
  ExternalTypes = [0]
  FullyConstrained = true
  MakeInternals = false
  MapMode = 5
  _ExternalGeoVersion = 0
  expr: Constraints[19] = <<sheet>>.BoxCornerRadius
  expr: Constraints[29] = <<sheet>>.PanelWidth
  expr: Constraints[30] = <<sheet>>.PanelLength
  expr: Constraints[31] = <<sheet>>.BoxAntennaSpace
  sketch-geometry (14):
    g0: LineSegment StartX=-49 StartY=41 StartZ=0 EndX=-49 EndY=-41 EndZ=0
    g1: LineSegment StartX=-47.5 StartY=-42.5 StartZ=0 EndX=47.5 EndY=-42.5 EndZ=0
    g2: LineSegment StartX=49 StartY=-41 StartZ=0 EndX=49 EndY=41 EndZ=0
    g3: LineSegment StartX=47.5 StartY=42.5 StartZ=0 EndX=-47.5 EndY=42.5 EndZ=0
    g4: ArcOfCircle CenterX=-47.5 CenterY=41 CenterZ=0 NormalX=0 NormalY=0 NormalZ=1 AngleXU=0 Radius=1.5 StartAngle=1.5708 EndAngle=3.14159
    g5: ArcOfCircle CenterX=-47.5 CenterY=-41 CenterZ=0 NormalX=0 NormalY=0 NormalZ=1 AngleXU=0 Radius=1.5 StartAngle=3.14159 EndAngle=4.71239
    g6: ArcOfCircle CenterX=47.5 CenterY=-41 CenterZ=0 NormalX=0 NormalY=0 NormalZ=1 AngleXU=0 Radius=1.5 StartAngle=4.71239 EndAngle=6.28319
    g7: ArcOfCircle CenterX=47.5 CenterY=41 CenterZ=0 NormalX=0 NormalY=0 NormalZ=1 AngleXU=0 Radius=1.5 StartAngle=2.2e-15 EndAngle=1.5708
    g8: GeomPoint [constr] X=-49 Y=42.5 Z=0
    g9: GeomPoint [constr] X=49 Y=-42.5 Z=0
    g10: LineSegment [constr] StartX=-47.5 StartY=-42.5 StartZ=0 EndX=47.5 EndY=-42.5 EndZ=0
    g11: LineSegment [constr] StartX=47.5 StartY=-42.5 StartZ=0 EndX=47.5 EndY=32.5 EndZ=0
    g12: LineSegment [constr] StartX=47.5 StartY=32.5 StartZ=0 EndX=-47.5 EndY=32.5 EndZ=0
    g13: LineSegment [constr] StartX=-47.5 StartY=32.5 StartZ=0 EndX=-47.5 EndY=-42.5 EndZ=0
  constraints (33):
    c: Tangent(g0,g4) = -1.5708
    c: Tangent(g0,g5) = -1.5708
    c: Tangent(g1,g5) = -1.5708
    c: Tangent(g1,g6) = -1.5708
    c: Tangent(g2,g6) = -1.5708
    c: Tangent(g2,g7) = -1.5708
    c: Tangent(g3,g7) = -1.5708
    c: Tangent(g3,g4) = -1.5708
    c: Vertical(g0)
    c: Vertical(g2)
    c: Horizontal(g1)
    c: Horizontal(g3)
    c: Equal(g4,g5)
    c: Equal(g5,g6)
    c: Equal(g6,g7)
    c: PointOnObject(g8,g0)
    c: PointOnObject(g8,g3)
    c: PointOnObject(g9,g1)
    c: PointOnObject(g9,g2)
    c: Radius(g5) = 1.5
    c: Coincident(g10,g11)
    c: Coincident(g11,g12)
    c: Coincident(g12,g13)
    c: Coincident(g13,g10)
    c: Horizontal(g12)
    c: Vertical(g11)
    c: Vertical(g13)
    c: Coincident(g10,g1)
    c: Coincident(g10,g1)
    c: DistanceY(g11,g11) = 75
    c: DistanceX(g12,g12) = 95
    c: DistanceY(g11,g3) = 10
    c: Symmetric(g3,g1,g-1)
FEATURE [PartDesign::Pad] Pad006  label="SealBase"
  Direction = (0,0,1)
  Length = 0.6
  Length2 = 10
  Profile = -> Sketch008
  ReferenceAxis = -> Sketch008 [N_Axis]
  SideType = 0
  Suppressed = false
  Type = 0
  Type2 = 0
FEATURE [Sketcher::SketchObject] Sketch009  label="SealTopSketch"
  ArcFitTolerance = 1e-06
  AttachmentSupport = -> [XY_Plane001]
  ExternalGeometry = -> [Sketch008]
  ExternalTypes = [0]
  FullyConstrained = true
  MakeInternals = false
  MapMode = 5
  _ExternalGeoVersion = 0
  expr: Constraints[10] = <<sheet>>.WallWidth
  expr: Constraints[11] = <<sheet>>.WallWidth
  expr: Constraints[44] = <<sheet>>.SealWidthTop + 0.1 mm
  expr: Constraints[45] = (<<sheet>>.WallWidth - <<sheet>>.SealWidthTop) / 2
  expr: Constraints[8] = <<sheet>>.WallWidth * 2
  expr: Constraints[9] = <<sheet>>.AntSmallLoraHeight + 1 mm + <<sheet>>.WallWidth * 2
  sketch-geometry (22):
    g0: LineSegment [constr] StartX=-44 StartY=30.1 StartZ=0 EndX=-44 EndY=-32.5 EndZ=0
    g1: LineSegment [constr] StartX=-44 StartY=-32.5 StartZ=0 EndX=44 EndY=-32.5 EndZ=0
    g2: LineSegment [constr] StartX=44 StartY=-32.5 StartZ=0 EndX=44 EndY=30.1 EndZ=0
    g3: LineSegment [constr] StartX=44 StartY=30.1 StartZ=0 EndX=-44 EndY=30.1 EndZ=0
    g4: LineSegment StartX=-45.9 StartY=30.1 StartZ=0 EndX=-45.9 EndY=-32.5 EndZ=0
    g5: LineSegment StartX=-44 StartY=-34.4 StartZ=0 EndX=44 EndY=-34.4 EndZ=0
    g6: LineSegment StartX=45.9 StartY=-32.5 StartZ=0 EndX=45.9 EndY=30.1 EndZ=0
    g7: LineSegment StartX=44 StartY=32 StartZ=0 EndX=-44 EndY=32 EndZ=0
    g8: ArcOfCircle CenterX=-44 CenterY=30.1 CenterZ=0 NormalX=0 NormalY=0 NormalZ=1 AngleXU=0 Radius=1.9 StartAngle=1.5708 EndAngle=3.14159
    g9: ArcOfCircle CenterX=-44 CenterY=-32.5 CenterZ=0 NormalX=0 NormalY=0 NormalZ=1 AngleXU=0 Radius=1.9 StartAngle=3.14159 EndAngle=4.71239
    g10: ArcOfCircle CenterX=44 CenterY=-32.5 CenterZ=0 NormalX=0 NormalY=0 NormalZ=1 AngleXU=0 Radius=1.9 StartAngle=4.71239 EndAngle=6.28319
    g11: ArcOfCircle CenterX=44 CenterY=30.1 CenterZ=0 NormalX=0 NormalY=0 NormalZ=1 AngleXU=0 Radius=1.9 StartAngle=-9e-16 EndAngle=1.5708
    g12: LineSegment StartX=-47.2 StartY=30.1 StartZ=0 EndX=-47.2 EndY=-32.5 EndZ=0
    g13: LineSegment StartX=-44 StartY=-35.7 StartZ=0 EndX=44 EndY=-35.7 EndZ=0
    g14: LineSegment StartX=47.2 StartY=-32.5 StartZ=0 EndX=47.2 EndY=30.1 EndZ=0
    g15: LineSegment StartX=44 StartY=33.3 StartZ=0 EndX=-44 EndY=33.3 EndZ=0
    g16: ArcOfCircle CenterX=-44 CenterY=30.1 CenterZ=0 NormalX=0 NormalY=0 NormalZ=1 AngleXU=0 Radius=3.2 StartAngle=1.5708 EndAngle=3.14159
    g17: ArcOfCircle CenterX=-44 CenterY=-32.5 CenterZ=0 NormalX=0 NormalY=0 NormalZ=1 AngleXU=0 Radius=3.2 StartAngle=3.14159 EndAngle=4.71239
    g18: ArcOfCircle CenterX=44 CenterY=-32.5 CenterZ=0 NormalX=0 NormalY=0 NormalZ=1 AngleXU=0 Radius=3.2 StartAngle=4.71239 EndAngle=6.28319
    g19: ArcOfCircle CenterX=44 CenterY=30.1 CenterZ=0 NormalX=0 NormalY=0 NormalZ=1 AngleXU=0 Radius=3.2 StartAngle=2e-16 EndAngle=1.5708
    g20: GeomPoint [constr] X=-45.9 Y=32 Z=0
    g21: GeomPoint [constr] X=45.9 Y=-34.4 Z=0
  constraints (49):
    c: Coincident(g0,g1)
    c: Coincident(g1,g2)
    c: Coincident(g2,g3)
    c: Coincident(g3,g0)
    c: Vertical(g0)
    c: Vertical(g2)
    c: Horizontal(g1)
    c: Horizontal(g3)
    c: DistanceY(g-4,g1) = 10
    c: DistanceY(g2,g-3) = 12.4
    c: DistanceX(g1,g-6) = 5
    c: DistanceX(g-5,g0) = 5
    c: Tangent(g4,g8) = -1.5708
    c: Tangent(g4,g9) = -1.5708
    c: Tangent(g5,g9) = -1.5708
    c: Tangent(g5,g10) = -1.5708
    c: Tangent(g6,g10) = -1.5708
    c: Tangent(g6,g11) = -1.5708
    c: Tangent(g7,g11) = -1.5708
    c: Tangent(g7,g8) = -1.5708
    c: Vertical(g4)
    c: Vertical(g6)
    c: Horizontal(g5)
    c: Horizontal(g7)
    c: Equal(g9,g10)
    c: Tangent(g12,g16) = -1.5708
    c: Tangent(g12,g17) = -1.5708
    c: Tangent(g13,g17) = -1.5708
    c: Tangent(g13,g18) = -1.5708
    c: Tangent(g14,g18) = -1.5708
    c: Tangent(g14,g19) = -1.5708
    c: Tangent(g15,g19) = -1.5708
    c: Tangent(g15,g16) = -1.5708
    c: Coincident(g8,g16)
    c: Coincident(g9,g17)
    c: Coincident(g10,g18)
    c: Coincident(g11,g19)
    c: Vertical(g12)
    c: Vertical(g14)
    c: Horizontal(g13)
    c: PointOnObject(g20,g4)
    c: PointOnObject(g20,g7)
    c: PointOnObject(g21,g5)
    c: PointOnObject(g21,g6)
    c: DistanceY(g7,g15) = 1.3
    c: DistanceY(g0,g7) = 1.9
    c: Coincident(g11,g2)
    c: Coincident(g0,g8)
    c: Coincident(g9,g0)
FEATURE [PartDesign::Plane] DatumPlane001  label="SealBottomPlane"
  AttachmentOffset = pos=(0,0,3) rot=(0,0,1;0rad)
  AttachmentSupport = -> [Pad006]
  Length = 118.873
  MapMode = 5
  Placement = pos=(0,0,3.6) rot=(0,0,1;0rad)
  ResizeMode = 0
  Width = 105.673
  expr: .AttachmentOffset.Base.z = <<sheet>>.SealHeight
FEATURE [Sketcher::SketchObject] Sketch010  label="SealBottomSketch"
  ArcFitTolerance = 1e-06
  AttachmentSupport = -> [DatumPlane001]
  ExternalGeometry = -> [Sketch009]
  ExternalTypes = [0]
  FullyConstrained = true
  MakeInternals = false
  MapMode = 5
  Placement = pos=(0,0,3.6) rot=(0,0,1;0rad)
  _ExternalGeoVersion = 0
  expr: Constraints[36] = <<sheet>>.SealWidthTop - 0.1 mm
  sketch-geometry (18):
    g0: LineSegment StartX=-45.9 StartY=30.1 StartZ=0 EndX=-45.9 EndY=-32.5 EndZ=0
    g1: LineSegment StartX=-44 StartY=-34.4 StartZ=0 EndX=44 EndY=-34.4 EndZ=0
    g2: LineSegment StartX=45.9 StartY=-32.5 StartZ=0 EndX=45.9 EndY=30.1 EndZ=0
    g3: LineSegment StartX=44 StartY=32 StartZ=0 EndX=-44 EndY=32 EndZ=0
    g4: ArcOfCircle CenterX=-44 CenterY=30.1 CenterZ=0 NormalX=0 NormalY=0 NormalZ=1 AngleXU=0 Radius=1.9 StartAngle=1.5708 EndAngle=3.14159
    g5: ArcOfCircle CenterX=-44 CenterY=-32.5 CenterZ=0 NormalX=0 NormalY=0 NormalZ=1 AngleXU=0 Radius=1.9 StartAngle=3.14159 EndAngle=4.71239
    g6: ArcOfCircle CenterX=44 CenterY=-32.5 CenterZ=0 NormalX=0 NormalY=0 NormalZ=1 AngleXU=0 Radius=1.9 StartAngle=4.71239 EndAngle=6.28319
    g7: ArcOfCircle CenterX=44 CenterY=30.1 CenterZ=0 NormalX=0 NormalY=0 NormalZ=1 AngleXU=0 Radius=1.9 StartAngle=-9e-16 EndAngle=1.5708
    g8: LineSegment StartX=-47 StartY=30.1 StartZ=0 EndX=-47 EndY=-32.5 EndZ=0
    g9: LineSegment StartX=-44 StartY=-35.5 StartZ=0 EndX=44 EndY=-35.5 EndZ=0
    g10: LineSegment StartX=47 StartY=-32.5 StartZ=0 EndX=47 EndY=30.1 EndZ=0
    g11: LineSegment StartX=44 StartY=33.1 StartZ=0 EndX=-44 EndY=33.1 EndZ=0
    g12: ArcOfCircle CenterX=-44 CenterY=30.1 CenterZ=0 NormalX=0 NormalY=0 NormalZ=1 AngleXU=0 Radius=3 StartAngle=1.5708 EndAngle=3.14159
    g13: ArcOfCircle CenterX=-44 CenterY=-32.5 CenterZ=0 NormalX=0 NormalY=0 NormalZ=1 AngleXU=0 Radius=3 StartAngle=3.14159 EndAngle=4.71239
    g14: ArcOfCircle CenterX=44 CenterY=-32.5 CenterZ=0 NormalX=0 NormalY=0 NormalZ=1 AngleXU=0 Radius=3 StartAngle=4.71239 EndAngle=6.28319
    g15: ArcOfCircle CenterX=44 CenterY=30.1 CenterZ=0 NormalX=0 NormalY=0 NormalZ=1 AngleXU=0 Radius=3 StartAngle=4e-16 EndAngle=1.5708
    g16: GeomPoint [constr] X=-45.9 Y=32 Z=0
    g17: GeomPoint [constr] X=45.9 Y=-34.4 Z=0
  constraints (37):
    c: Tangent(g0,g4) = -1.5708
    c: Tangent(g0,g5) = -1.5708
    c: Tangent(g1,g5) = -1.5708
    c: Tangent(g1,g6) = -1.5708
    c: Tangent(g2,g6) = -1.5708
    c: Tangent(g2,g7) = -1.5708
    c: Tangent(g3,g7) = -1.5708
    c: Tangent(g3,g4) = -1.5708
    c: Vertical(g0)
    c: Vertical(g2)
    c: Horizontal(g1)
    c: Equal(g4,g5)
    c: Equal(g5,g6)
    c: Equal(g6,g7)
    c: Tangent(g8,g12) = -1.5708
    c: Tangent(g8,g13) = -1.5708
    c: Tangent(g9,g13) = -1.5708
    c: Tangent(g9,g14) = -1.5708
    c: Tangent(g10,g14) = -1.5708
    c: Tangent(g10,g15) = -1.5708
    c: Tangent(g11,g15) = -1.5708
    c: Tangent(g11,g12) = -1.5708
    c: Coincident(g4,g12)
    c: Coincident(g5,g13)
    c: Coincident(g6,g14)
    c: Coincident(g7,g15)
    c: Vertical(g8)
    c: Vertical(g10)
    c: Horizontal(g9)
    c: PointOnObject(g16,g0)
    c: PointOnObject(g16,g3)
    c: PointOnObject(g17,g1)
    c: PointOnObject(g17,g2)
    c: Coincident(g2,g-3)
    c: Coincident(g3,g-4)
    c: Coincident(g3,g-4)
    c: DistanceY(g3,g11) = 1.1
FEATURE [PartDesign::AdditiveLoft] AdditiveLoft  label="SealSeal"
  BaseFeature = -> Pad006
  Closed = false
  Profile = -> Sketch009
  Ruled = false
  Sections = -> [Sketch010]
  Suppressed = false
FEATURE [PartDesign::SubShapeBinder] Binder  label="SealBoxBinder"
  BindCopyOnChange = 0
  BindMode = 0
  ClaimChildren = false
  Context = -> Body001 [Binder.]
  Fuse = false
  MakeFace = true
  OffsetFill = false
  OffsetIntersection = false
  OffsetJoinType = 0
  OffsetOpenResult = false
  PartialLoad = false
  Relative = true
  Support = -> [Body[Pocket001.]]
  _Version = 2
FEATURE [Sketcher::SketchObject] Sketch011  label="SealBoxLidHolesSketch"
  ArcFitTolerance = 1e-06
  AttachmentSupport = -> [XY_Plane001]
  ExternalGeometry = -> [Binder]
  ExternalTypes = [0]
  FullyConstrained = true
  MakeInternals = false
  MapMode = 5
  _ExternalGeoVersion = 0
  sketch-geometry (7):
    g0: Circle CenterX=-44 CenterY=-39.1667 CenterZ=0 NormalX=0 NormalY=0 NormalZ=1 AngleXU=0 Radius=1.5
    g1: Circle CenterX=-29 CenterY=-39.1667 CenterZ=0 NormalX=0 NormalY=0 NormalZ=1 AngleXU=0 Radius=1.5
    g2: Circle CenterX=31 CenterY=-39.1667 CenterZ=0 NormalX=0 NormalY=0 NormalZ=1 AngleXU=0 Radius=1.5
    g3: Circle CenterX=-29 CenterY=36.7667 CenterZ=0 NormalX=0 NormalY=0 NormalZ=1 AngleXU=0 Radius=1.5
    g4: Circle CenterX=31 CenterY=36.7667 CenterZ=0 NormalX=0 NormalY=0 NormalZ=1 AngleXU=0 Radius=1.5
    g5: Circle CenterX=44 CenterY=36.7667 CenterZ=0 NormalX=0 NormalY=0 NormalZ=1 AngleXU=0 Radius=1.5
    g6: Circle CenterX=44 CenterY=-39.1667 CenterZ=0 NormalX=0 NormalY=0 NormalZ=1 AngleXU=0 Radius=1.5
  constraints (14):
    c: Diameter(g0) = 3
    c: Equal(g0,g1)
    c: Equal(g1,g2)
    c: Equal(g2,g6)
    c: Equal(g6,g5)
    c: Equal(g5,g4)
    c: Equal(g4,g3)
    c: Coincident(g6,g-8)
    c: Coincident(g2,g-9)
    c: Coincident(g1,g-3)
    c: Coincident(g0,g-4)
    c: Coincident(g3,g-5)
    c: Coincident(g4,g-6)
    c: Coincident(g5,g-7)
FEATURE [PartDesign::Pocket] Pocket002  label="SealBoxLidHoles"
  BaseFeature = -> AdditiveLoft
  Direction = (0,0,-1)
  Length = 0.6
  Length2 = 5
  Profile = -> Sketch011
  ReferenceAxis = -> Sketch011 [N_Axis]
  Reversed = true
  SideType = 0
  Suppressed = false
  Type = 0
  Type2 = 0
  expr: Length = <<SealBase>>.Length
FEATURE [Sketcher::SketchObject] Sketch012  label="SealInnserSealSketch"
  ArcFitTolerance = 1e-06
  AttachmentSupport = -> [XY_Plane001]
  ExternalGeometry = -> [Binder]
  ExternalTypes = [0]
  FullyConstrained = true
  MakeInternals = false
  MapMode = 5
  _ExternalGeoVersion = 0
  expr: Constraints[10] = <<sheet>>.SealWidthTop
  expr: Constraints[11] = <<sheet>>.SealWidthTop
  expr: Constraints[12] = <<sheet>>.SealWidthTop
  expr: Constraints[45] = <<sheet>>.SealWidthTop
  expr: Constraints[59] = <<sheet>>.SealWidthTop
  expr: Constraints[60] = <<sheet>>.SealWidthTop
  expr: Constraints[61] = <<sheet>>.BatteryMountDistance
  expr: Constraints[64] = <<sheet>>.SealWidthTop
  expr: Constraints[65] = <<sheet>>.BatteryWidth
  sketch-geometry (24):
    g0: LineSegment StartX=44 StartY=30.1 StartZ=0 EndX=44 EndY=-14.5 EndZ=0
    g1: LineSegment StartX=-44 StartY=-14.5 StartZ=0 EndX=-44 EndY=30.1 EndZ=0
    g2: LineSegment StartX=-42.8 StartY=28.9 StartZ=0 EndX=42.8 EndY=28.9 EndZ=0
    g3: LineSegment StartX=42.8 StartY=28.9 StartZ=0 EndX=42.8 EndY=-13.3 EndZ=0
    g4: LineSegment StartX=36.3 StartY=-13.3 StartZ=0 EndX=36.3 EndY=-31.3 EndZ=0
    g5: LineSegment StartX=36.3 StartY=-31.3 StartZ=0 EndX=-36.3 EndY=-31.3 EndZ=0
    g6: LineSegment StartX=-36.3 StartY=-31.3 StartZ=0 EndX=-36.3 EndY=-13.3 EndZ=0
    g7: LineSegment StartX=-42.8 StartY=28.9 StartZ=0 EndX=-42.8 EndY=-13.3 EndZ=0
    g8: LineSegment StartX=-44 StartY=30.1 StartZ=0 EndX=-41 EndY=30.1 EndZ=0
    g9: LineSegment StartX=-41 StartY=30.1 StartZ=0 EndX=-41 EndY=33.5 EndZ=0
    g10: LineSegment StartX=-41 StartY=33.5 StartZ=0 EndX=-39.5 EndY=33.5 EndZ=0
    g11: LineSegment StartX=-39.5 StartY=33.5 StartZ=0 EndX=-39.5 EndY=30.1 EndZ=0
    g12: LineSegment StartX=-39.5 StartY=30.1 StartZ=0 EndX=7.05 EndY=30.1 EndZ=0
    g13: LineSegment StartX=7.05 StartY=30.1 StartZ=0 EndX=7.05 EndY=39.35 EndZ=0
    g14: LineSegment StartX=7.05 StartY=39.35 StartZ=0 EndX=8.45 EndY=39.35 EndZ=0
    g15: LineSegment StartX=8.45 StartY=39.35 StartZ=0 EndX=8.45 EndY=30.1 EndZ=0
    g16: LineSegment StartX=44 StartY=30.1 StartZ=0 EndX=8.45 EndY=30.1 EndZ=0
    g17: LineSegment StartX=-37.5 StartY=-14.5 StartZ=0 EndX=-37.5 EndY=-32.5 EndZ=0
    g18: LineSegment StartX=-37.5 StartY=-32.5 StartZ=0 EndX=37.5 EndY=-32.5 EndZ=0
    g19: LineSegment StartX=37.5 StartY=-32.5 StartZ=0 EndX=37.5 EndY=-14.5 EndZ=0
    g20: LineSegment StartX=-36.3 StartY=-13.3 StartZ=0 EndX=-42.8 EndY=-13.3 EndZ=0
    g21: LineSegment StartX=-44 StartY=-14.5 StartZ=0 EndX=-37.5 EndY=-14.5 EndZ=0
    g22: LineSegment StartX=36.3 StartY=-13.3 StartZ=0 EndX=42.8 EndY=-13.3 EndZ=0
    g23: LineSegment StartX=37.5 StartY=-14.5 StartZ=0 EndX=44 EndY=-14.5 EndZ=0
  constraints (66):
    c: Horizontal(g2)
    c: Coincident(g3,g2)
    c: Vertical(g3)
    c: Coincident(g5,g4)
    c: Horizontal(g5)
    c: Coincident(g6,g5)
    c: Coincident(g7,g2)
    c: Vertical(g7)
    c: Vertical(g4)
    c: Vertical(g6)
    c: DistanceY(g2,g-3) = 1.2
    c: DistanceX(g3,g0) = 1.2
    c: DistanceY(g0,g3) = 1.2
    c: Coincident(g1,g8)
    c: Horizontal(g8)
    c: Coincident(g8,g9)
    c: Coincident(g9,g-5)
    c: Vertical(g9)
    c: Coincident(g9,g10)
    c: Coincident(g10,g-8)
    c: Coincident(g10,g11)
    c: Vertical(g11)
    c: Vertical(g0)
    c: Horizontal(g8,g11)
    c: Coincident(g1,g-3)
    c: Coincident(g12,g11)
    c: Horizontal(g12)
    c: Coincident(g13,g12)
    c: Vertical(g13)
    c: Coincident(g14,g13)
    c: Horizontal(g14)
    c: Coincident(g15,g14)
    c: Vertical(g15)
    c: Coincident(g16,g0)
    c: Coincident(g16,g15)
    c: Horizontal(g16)
    c: Horizontal(g15,g12)
    c: Horizontal(g13,g-6)
    c: DistanceX(g-6,g13) = 0.05
    c: Distance(g14,g-7) = 0.05
    c: Coincident(g18,g17)
    c: Horizontal(g18)
    c: Coincident(g19,g18)
    c: Vertical(g19)
    c: Vertical(g17)
    c: DistanceY(g17,g5) = 1.2
    c: Coincident(g20,g6)
    c: Coincident(g20,g7)
    c: Horizontal(g20)
    c: Coincident(g21,g1)
    c: Coincident(g21,g17)
    c: Horizontal(g21)
    c: Coincident(g22,g4)
    c: Coincident(g22,g3)
    c: Horizontal(g22)
    c: Coincident(g23,g19)
    c: Coincident(g23,g0)
    c: Horizontal(g23)
    c: Symmetric(g6,g4,g-2)
    c: DistanceX(g17,g6) = 1.2
    c: DistanceX(g4,g19) = 1.2
    c: DistanceX(g17,g19) = 75
    c: Coincident(g1,g-3)
    c: Coincident(g0,g-4)
    c: DistanceX(g1,g7) = 1.2
    c: DistanceY(g4,g4) = 18
FEATURE [PartDesign::Pad] Pad007  label="SealInnerSeal"
  BaseFeature = -> Pocket002
  Direction = (0,0,1)
  Length = 3.6
  Length2 = 10
  Profile = -> Sketch012
  ReferenceAxis = -> Sketch012 [N_Axis]
  SideType = 0
  Suppressed = false
  Type = 0
  Type2 = 0
  expr: Length = <<sheet>>.SealHeight + <<SealBase>>.Length
FEATURE [PartDesign::SubShapeBinder] Binder001  label="LidBoxBinder"
  BindCopyOnChange = 0
  BindMode = 0
  ClaimChildren = false
  Context = -> Body002 [Binder001.]
  Fuse = false
  MakeFace = true
  OffsetFill = false
  OffsetIntersection = false
  OffsetJoinType = 0
  OffsetOpenResult = false
  PartialLoad = false
  Relative = true
  Support = -> [Body[Pocket001.]]
  _Version = 2
FEATURE [Sketcher::SketchObject] Sketch013  label="LidBaseSketch"
  ArcFitTolerance = 1e-06
  AttachmentSupport = -> [XY_Plane002]
  ExternalGeometry = -> [Binder001]
  ExternalTypes = [0]
  FullyConstrained = true
  MakeInternals = false
  MapMode = 5
  _ExternalGeoVersion = 0
  expr: Constraints[33] = <<sheet>>.SealOuterWidth
  expr: Constraints[34] = <<sheet>>.SealOuterWidth
  expr: Constraints[35] = <<sheet>>.BoxCornerRadius
  expr: Constraints[36] = <<sheet>>.SealOuterWidth
  expr: Constraints[37] = <<sheet>>.SealOuterWidth
  sketch-geometry (17):
    g0: Circle CenterX=-44 CenterY=36.7667 CenterZ=0 NormalX=0 NormalY=0 NormalZ=1 AngleXU=0 Radius=1.65
    g1: Circle CenterX=-31 CenterY=36.7667 CenterZ=0 NormalX=0 NormalY=0 NormalZ=1 AngleXU=0 Radius=1.65
    g2: Circle CenterX=29 CenterY=36.7667 CenterZ=0 NormalX=0 NormalY=0 NormalZ=1 AngleXU=0 Radius=1.65
    g3: Circle CenterX=44 CenterY=-39.1667 CenterZ=0 NormalX=0 NormalY=0 NormalZ=1 AngleXU=0 Radius=1.65
    g4: Circle CenterX=29 CenterY=-39.1667 CenterZ=0 NormalX=0 NormalY=0 NormalZ=1 AngleXU=0 Radius=1.65
    g5: Circle CenterX=-31 CenterY=-39.1667 CenterZ=0 NormalX=0 NormalY=0 NormalZ=1 AngleXU=0 Radius=1.65
    g6: Circle CenterX=-44 CenterY=-39.1667 CenterZ=0 NormalX=0 NormalY=0 NormalZ=1 AngleXU=0 Radius=1.65
    g7: LineSegment StartX=-50 StartY=42 StartZ=0 EndX=-50 EndY=-42 EndZ=0
    g8: LineSegment StartX=-48.5 StartY=-43.5 StartZ=0 EndX=48.5 EndY=-43.5 EndZ=0
    g9: LineSegment StartX=50 StartY=-42 StartZ=0 EndX=50 EndY=42 EndZ=0
    g10: LineSegment StartX=48.5 StartY=43.5 StartZ=0 EndX=-48.5 EndY=43.5 EndZ=0
    g11: ArcOfCircle CenterX=-48.5 CenterY=42 CenterZ=0 NormalX=0 NormalY=0 NormalZ=1 AngleXU=0 Radius=1.5 StartAngle=1.5708 EndAngle=3.14159
    g12: ArcOfCircle CenterX=-48.5 CenterY=-42 CenterZ=0 NormalX=0 NormalY=0 NormalZ=1 AngleXU=0 Radius=1.5 StartAngle=3.14159 EndAngle=4.71239
    g13: ArcOfCircle CenterX=48.5 CenterY=-42 CenterZ=0 NormalX=0 NormalY=0 NormalZ=1 AngleXU=0 Radius=1.5 StartAngle=4.71239 EndAngle=6.28319
    g14: ArcOfCircle CenterX=48.5 CenterY=42 CenterZ=0 NormalX=0 NormalY=0 NormalZ=1 AngleXU=0 Radius=1.5 StartAngle=2.95e-13 EndAngle=1.5708
    g15: GeomPoint [constr] X=-50 Y=43.5 Z=0
    g16: GeomPoint [constr] X=50 Y=-43.5 Z=0
  constraints (38):
    c: Coincident(g0,g-4)
    c: Coincident(g1,g-5)
    c: Coincident(g2,g-6)
    c: Coincident(g3,g-8)
    c: Coincident(g4,g-7)
    c: Coincident(g5,g-10)
    c: Coincident(g6,g-9)
    c: Diameter(g0) = 3.3
    c: Equal(g0,g1)
    c: Equal(g1,g2)
    c: Equal(g2,g6)
    c: Equal(g6,g5)
    c: Equal(g5,g4)
    c: Equal(g4,g3)
    c: Tangent(g7,g11) = -1.5708
    c: Tangent(g7,g12) = -1.5708
    c: Tangent(g8,g12) = -1.5708
    c: Tangent(g8,g13) = -1.5708
    c: Tangent(g9,g13) = -1.5708
    c: Tangent(g9,g14) = -1.5708
    c: Tangent(g10,g14) = -1.5708
    c: Tangent(g10,g11) = -1.5708
    c: Vertical(g7)
    c: Vertical(g9)
    c: Horizontal(g8)
    c: Horizontal(g10)
    c: Equal(g11,g12)
    c: Equal(g12,g13)
    c: Equal(g13,g14)
    c: PointOnObject(g15,g7)
    c: PointOnObject(g15,g10)
    c: PointOnObject(g16,g8)
    c: PointOnObject(g16,g9)
    c: DistanceY(g-3,g10) = 1
    c: DistanceX(g-13,g9) = 1
    c: Radius(g14) = 1.5
    c: DistanceX(g7,g-11) = 1
    c: DistanceY(g8,g-12) = 1
FEATURE [PartDesign::Pad] Pad008  label="LidBase"
  Direction = (0,0,1)
  Length = 1
  Length2 = 10
  Profile = -> Sketch013
  ReferenceAxis = -> Sketch013 [N_Axis]
  SideType = 0
  Suppressed = false
  Type = 0
  Type2 = 0
  expr: Length = <<sheet>>.WallBottomThickness
FEATURE [PartDesign::SubShapeBinder] Binder002  label="StrapBoxBinder"
  BindCopyOnChange = 0
  BindMode = 0
  ClaimChildren = false
  Context = -> Body003 [Binder002.]
  Fuse = false
  MakeFace = true
  OffsetFill = false
  OffsetIntersection = false
  OffsetJoinType = 0
  OffsetOpenResult = false
  PartialLoad = false
  Relative = true
  Support = -> [Body[Pocket001.]]
  _Version = 2
FEATURE [Sketcher::SketchObject] Sketch014  label="StrapBaseSketch"
  ArcFitTolerance = 1e-06
  AttachmentSupport = -> [XY_Plane003]
  ExternalGeometry = -> [Binder002]
  ExternalTypes = [0]
  FullyConstrained = true
  MakeInternals = false
  MapMode = 5
  _ExternalGeoVersion = 0
  sketch-geometry (10):
    g0: LineSegment StartX=-49 StartY=41 StartZ=0 EndX=-49 EndY=-41 EndZ=0
    g1: LineSegment StartX=-47.5 StartY=-42.5 StartZ=0 EndX=47.5 EndY=-42.5 EndZ=0
    g2: LineSegment StartX=49 StartY=-41 StartZ=0 EndX=49 EndY=41 EndZ=0
    g3: LineSegment StartX=47.5 StartY=42.5 StartZ=0 EndX=-47.5 EndY=42.5 EndZ=0
    g4: ArcOfCircle CenterX=-47.5 CenterY=41 CenterZ=0 NormalX=0 NormalY=0 NormalZ=1 AngleXU=0 Radius=1.5 StartAngle=1.5708 EndAngle=3.14159
    g5: ArcOfCircle CenterX=-47.5 CenterY=-41 CenterZ=0 NormalX=0 NormalY=0 NormalZ=1 AngleXU=0 Radius=1.5 StartAngle=3.14159 EndAngle=4.71239
    g6: ArcOfCircle CenterX=47.5 CenterY=-41 CenterZ=0 NormalX=0 NormalY=0 NormalZ=1 AngleXU=0 Radius=1.5 StartAngle=4.71239 EndAngle=6.28319
    g7: ArcOfCircle CenterX=47.5 CenterY=41 CenterZ=0 NormalX=0 NormalY=0 NormalZ=1 AngleXU=0 Radius=1.5 StartAngle=0 EndAngle=1.5708
    g8: GeomPoint [constr] X=-49 Y=42.5 Z=0
    g9: GeomPoint [constr] X=49 Y=-42.5 Z=0
  constraints (21):
    c: Tangent(g0,g4) = -1.5708
    c: Tangent(g0,g5) = -1.5708
    c: Tangent(g1,g5) = -1.5708
    c: Tangent(g1,g6) = -1.5708
    c: Tangent(g2,g6) = -1.5708
    c: Tangent(g2,g7) = -1.5708
    c: Tangent(g3,g7) = -1.5708
    c: Tangent(g3,g4) = -1.5708
    c: Vertical(g0)
    c: Vertical(g2)
    c: Horizontal(g1)
    c: Horizontal(g3)
    c: Equal(g5,g6)
    c: Equal(g6,g7)
    c: PointOnObject(g8,g0)
    c: PointOnObject(g8,g3)
    c: PointOnObject(g9,g1)
    c: PointOnObject(g9,g2)
    c: Coincident(g-3,g3)
    c: Coincident(g2,g-4)
    c: Coincident(g1,g-5)
FEATURE [PartDesign::Pad] Pad009  label="StrapBase"
  Direction = (0,0,1)
  Length = 1.5
  Length2 = 10
  Profile = -> Sketch014
  ReferenceAxis = -> Sketch014 [N_Axis]
  Reversed = true
  SideType = 0
  Suppressed = false
  Type = 0
  Type2 = 0
FEATURE [Sketcher::SketchObject] Sketch015
  ArcFitTolerance = 1e-06
  AttachmentSupport = -> [XY_Plane003]
  ExternalGeometry = -> [Binder002]
  ExternalTypes = [0]
  FullyConstrained = true
  MakeInternals = false
  MapMode = 5
  _ExternalGeoVersion = 0
  sketch-geometry (7):
    g0: Circle CenterX=-44 CenterY=36.7667 CenterZ=0 NormalX=0 NormalY=0 NormalZ=1 AngleXU=0 Radius=3.25
    g1: Circle CenterX=-31 CenterY=36.7667 CenterZ=0 NormalX=0 NormalY=0 NormalZ=1 AngleXU=0 Radius=3.25
    g2: Circle CenterX=29 CenterY=36.7667 CenterZ=0 NormalX=0 NormalY=0 NormalZ=1 AngleXU=0 Radius=3.25
    g3: Circle CenterX=-44 CenterY=-39.1667 CenterZ=0 NormalX=0 NormalY=0 NormalZ=1 AngleXU=0 Radius=3.25
    g4: Circle CenterX=-31 CenterY=-39.1667 CenterZ=0 NormalX=0 NormalY=0 NormalZ=1 AngleXU=0 Radius=3.25
    g5: Circle CenterX=29 CenterY=-39.1667 CenterZ=0 NormalX=0 NormalY=0 NormalZ=1 AngleXU=0 Radius=3.25
    g6: Circle CenterX=44 CenterY=-39.1667 CenterZ=0 NormalX=0 NormalY=0 NormalZ=1 AngleXU=0 Radius=3.25
  constraints (14):
    c: Coincident(g0,g-3)
    c: Coincident(g1,g-4)
    c: Coincident(g2,g-5)
    c: Coincident(g3,g-9)
    c: Coincident(g4,g-8)
    c: Coincident(g5,g-7)
    c: Coincident(g6,g-6)
    c: Diameter(g0) = 6.5
    c: Equal(g0,g1)
    c: Equal(g1,g2)
    c: Equal(g2,g3)
    c: Equal(g3,g4)
    c: Equal(g4,g5)
    c: Equal(g5,g6)
FEATURE [PartDesign::Pad] Pad010
  BaseFeature = -> Pad009
  Direction = (0,0,1)
  Length = 2.8
  Length2 = 10
  Profile = -> Sketch015
  ReferenceAxis = -> Sketch015 [N_Axis]
  Reversed = true
  SideType = 0
  Suppressed = false
  Type = 0
  Type2 = 0
FEATURE [PartDesign::Hole] Hole
  BaseFeature = -> Pad010
  BaseProfileType = 6
  CustomThreadClearance = 0
  Depth = 25
  DepthType = 0
  Diameter = 3.4
  DrillForDepth = false
  DrillPoint = 1
  DrillPointAngle = 118
  HoleCutCountersinkAngle = 90
  HoleCutCustomValues = false
  HoleCutDepth = 3.05
  HoleCutDiameter = 6.1
  HoleCutType = 2
  ModelThread = false
  Profile = -> Sketch015
  Suppressed = false
  Tapered = false
  TaperedAngle = 90
  ThreadClass = 0
  ThreadDepth = 25
  ThreadDepthType = 0
  ThreadDiameter = 3
  ThreadDirection = 0
  ThreadFit = 0
  ThreadSize = 9
  ThreadType = 2
  Threaded = false
  UseCustomThreadClearance = false
FEATURE [Sketcher::SketchObject] Sketch016
  ArcFitTolerance = 1e-06
  AttachmentSupport = -> [Hole]
  ExternalTypes = [0]
  FullyConstrained = true
  MakeInternals = false
  MapMode = 5
  _ExternalGeoVersion = 0
  sketch-geometry (16):
    g0: ArcOfCircle CenterX=-25 CenterY=30 CenterZ=0 NormalX=0 NormalY=0 NormalZ=1 AngleXU=0 Radius=2 StartAngle=1.5708 EndAngle=4.71239
    g1: ArcOfCircle CenterX=25 CenterY=30 CenterZ=0 NormalX=0 NormalY=0 NormalZ=1 AngleXU=0 Radius=2 StartAngle=4.71239 EndAngle=7.85398
    g2: LineSegment StartX=-25 StartY=32 StartZ=0 EndX=25 EndY=32 EndZ=0
    g3: LineSegment StartX=-25 StartY=28 StartZ=0 EndX=25 EndY=28 EndZ=0
    g4: ArcOfCircle CenterX=-25 CenterY=-30 CenterZ=0 NormalX=0 NormalY=0 NormalZ=1 AngleXU=0 Radius=2 StartAngle=1.5708 EndAngle=4.71239
    g5: ArcOfCircle CenterX=25 CenterY=-30 CenterZ=0 NormalX=0 NormalY=0 NormalZ=1 AngleXU=0 Radius=2 StartAngle=4.71239 EndAngle=7.85398
    g6: LineSegment StartX=-25 StartY=-28 StartZ=0 EndX=25 EndY=-28 EndZ=0
    g7: LineSegment StartX=-25 StartY=-32 StartZ=0 EndX=25 EndY=-32 EndZ=0
    g8: ArcOfCircle CenterX=-25 CenterY=20 CenterZ=0 NormalX=0 NormalY=0 NormalZ=1 AngleXU=0 Radius=2 StartAngle=1.5708 EndAngle=4.71239
    g9: ArcOfCircle CenterX=25 CenterY=20 CenterZ=0 NormalX=0 NormalY=0 NormalZ=1 AngleXU=0 Radius=2 StartAngle=4.71239 EndAngle=7.85398
    g10: LineSegment StartX=-25 StartY=22 StartZ=0 EndX=25 EndY=22 EndZ=0
    g11: LineSegment StartX=-25 StartY=18 StartZ=0 EndX=25 EndY=18 EndZ=0
    g12: ArcOfCircle CenterX=-25 CenterY=-20 CenterZ=0 NormalX=0 NormalY=0 NormalZ=1 AngleXU=0 Radius=2 StartAngle=1.5708 EndAngle=4.71239
    g13: ArcOfCircle CenterX=25 CenterY=-20 CenterZ=0 NormalX=0 NormalY=0 NormalZ=1 AngleXU=0 Radius=2 StartAngle=4.71239 EndAngle=7.85398
    g14: LineSegment StartX=-25 StartY=-18 StartZ=0 EndX=25 EndY=-18 EndZ=0
    g15: LineSegment StartX=-25 StartY=-22 StartZ=0 EndX=25 EndY=-22 EndZ=0
  constraints (38):
    c: Tangent(g0,g2) = 1.5708
    c: Tangent(g0,g3) = -1.5708
    c: Tangent(g1,g2) = 1.5708
    c: Tangent(g1,g3) = -1.5708
    c: Equal(g0,g1)
    c: Tangent(g4,g6) = 1.5708
    c: Tangent(g4,g7) = -1.5708
    c: Tangent(g5,g6) = 1.5708
    c: Tangent(g5,g7) = -1.5708
    c: Equal(g4,g5)
    c: Symmetric(g1,g0,g-2)
    c: Symmetric(g5,g4,g-2)
    c: DistanceX(g0,g1) = 50
    c: Vertical(g0,g4)
    c: Distance(g1,g1) = 4
    c: DistanceY(g5,g5) = 4
    c: Tangent(g8,g10) = 1.5708
    c: Tangent(g8,g11) = -1.5708
    c: Tangent(g9,g10) = 1.5708
    c: Tangent(g9,g11) = -1.5708
    c: Equal(g8,g9)
    c: Horizontal(g10)
    c: Tangent(g12,g14) = 1.5708
    c: Tangent(g12,g15) = -1.5708
    c: Tangent(g13,g14) = 1.5708
    c: Tangent(g13,g15) = -1.5708
    c: Equal(g12,g13)
    c: Horizontal(g14)
    c: Vertical(g1,g9)
    c: Vertical(g9,g13)
    c: Vertical(g8,g12)
    c: Vertical(g0,g8)
    c: DistanceY(g9,g9) = 4
    c: DistanceY(g13,g13) = 4
    c: DistanceY(g12,g-1) = 20
    c: DistanceY(g-1,g8) = 20
    c: DistanceY(g-1,g0) = 30
    c: DistanceY(g4,g-1) = 30
FEATURE [PartDesign::Pocket] Pocket003
  BaseFeature = -> Hole
  Direction = (0,0,-1)
  Length = 1.5
  Length2 = 5
  Profile = -> Sketch016
  ReferenceAxis = -> Sketch016 [N_Axis]
  SideType = 0
  Suppressed = false
  Type = 0
  Type2 = 0
  expr: Length = <<StrapBase>>.Length
FEATURE [PartDesign::Body] Body003  label="Strap"
  AllowCompound = false
  Group = -> [Sketch014,Binder002,Pad009,Sketch015,Pad010,Hole,Sketch016,Pocket003]
  Origin = -> Origin003
  Placement = pos=(0,0,63.5) rot=(0,0,1;0rad)
  Tip = -> Pocket003
FEATURE [Sketcher::SketchObject] Sketch018
  ArcFitTolerance = 1e-06
  AttachmentOffset = pos=(0,0,1) rot=(0,0,1;0rad)
  AttachmentSupport = -> [XY_Plane002]
  ExternalGeometry = -> [Sketch013]
  ExternalTypes = [0]
  FullyConstrained = true
  MakeInternals = false
  MapMode = 5
  Placement = pos=(0,0,1) rot=(0,0,1;0rad)
  _ExternalGeoVersion = 0
  expr: Constraints[33] = <<sheet>>.SealOuterWidth
  sketch-geometry (18):
    g0: LineSegment StartX=-50 StartY=42 StartZ=0 EndX=-50 EndY=-42 EndZ=0
    g1: LineSegment StartX=-48.5 StartY=-43.5 StartZ=0 EndX=48.5 EndY=-43.5 EndZ=0
    g2: LineSegment StartX=50 StartY=-42 StartZ=0 EndX=50 EndY=42 EndZ=0
    g3: LineSegment StartX=48.5 StartY=43.5 StartZ=0 EndX=-48.5 EndY=43.5 EndZ=0
    g4: ArcOfCircle CenterX=-48.5 CenterY=42 CenterZ=0 NormalX=0 NormalY=0 NormalZ=1 AngleXU=0 Radius=1.5 StartAngle=1.5708 EndAngle=3.14159
    g5: ArcOfCircle CenterX=-48.5 CenterY=-42 CenterZ=0 NormalX=0 NormalY=0 NormalZ=1 AngleXU=0 Radius=1.5 StartAngle=3.14159 EndAngle=4.71239
    g6: ArcOfCircle CenterX=48.5 CenterY=-42 CenterZ=0 NormalX=0 NormalY=0 NormalZ=1 AngleXU=0 Radius=1.5 StartAngle=4.71239 EndAngle=6.28319
    g7: ArcOfCircle CenterX=48.5 CenterY=42 CenterZ=0 NormalX=0 NormalY=0 NormalZ=1 AngleXU=0 Radius=1.5 StartAngle=1.233e-13 EndAngle=1.5708
    g8: LineSegment StartX=-51 StartY=42 StartZ=0 EndX=-51 EndY=-42 EndZ=0
    g9: LineSegment StartX=-48.5 StartY=-44.5 StartZ=0 EndX=48.5 EndY=-44.5 EndZ=0
    g10: LineSegment StartX=51 StartY=-42 StartZ=0 EndX=51 EndY=42 EndZ=0
    g11: LineSegment StartX=48.5 StartY=44.5 StartZ=0 EndX=-48.5 EndY=44.5 EndZ=0
    g12: ArcOfCircle CenterX=-48.5 CenterY=42 CenterZ=0 NormalX=0 NormalY=0 NormalZ=1 AngleXU=0 Radius=2.5 StartAngle=1.5708 EndAngle=3.14159
    g13: ArcOfCircle CenterX=-48.5 CenterY=-42 CenterZ=0 NormalX=0 NormalY=0 NormalZ=1 AngleXU=0 Radius=2.5 StartAngle=3.14159 EndAngle=4.71239
    g14: ArcOfCircle CenterX=48.5 CenterY=-42 CenterZ=0 NormalX=0 NormalY=0 NormalZ=1 AngleXU=0 Radius=2.5 StartAngle=4.71239 EndAngle=6.28319
    g15: ArcOfCircle CenterX=48.5 CenterY=42 CenterZ=0 NormalX=0 NormalY=0 NormalZ=1 AngleXU=0 Radius=2.5 StartAngle=-9e-16 EndAngle=1.5708
    g16: GeomPoint [constr] X=-50 Y=43.5 Z=0
    g17: GeomPoint [constr] X=50 Y=-43.5 Z=0
  constraints (36):
    c: Tangent(g0,g4) = -1.5708
    c: Tangent(g0,g5) = -1.5708
    c: Tangent(g1,g5) = -1.5708
    c: Tangent(g1,g6) = -1.5708
    c: Tangent(g2,g6) = -1.5708
    c: Tangent(g2,g7) = -1.5708
    c: Tangent(g3,g7) = -1.5708
    c: Tangent(g3,g4) = -1.5708
    c: Vertical(g2)
    c: Horizontal(g1)
    c: Equal(g5,g6)
    c: Equal(g6,g7)
    c: Tangent(g8,g12) = -1.5708
    c: Tangent(g8,g13) = -1.5708
    c: Tangent(g9,g13) = -1.5708
    c: Tangent(g9,g14) = -1.5708
    c: Tangent(g10,g14) = -1.5708
    c: Tangent(g10,g15) = -1.5708
    c: Tangent(g11,g15) = -1.5708
    c: Tangent(g11,g12) = -1.5708
    c: Coincident(g4,g12)
    c: Coincident(g5,g13)
    c: Coincident(g6,g14)
    c: Coincident(g7,g15)
    c: Vertical(g8)
    c: Vertical(g10)
    c: Horizontal(g9)
    c: PointOnObject(g16,g0)
    c: PointOnObject(g16,g3)
    c: PointOnObject(g17,g1)
    c: PointOnObject(g17,g2)
    c: Coincident(g-3,g3)
    c: Coincident(g3,g-3)
    c: DistanceY(g3,g11) = 1
    c: Coincident(g0,g-5)
    c: Coincident(g-4,g1)
FEATURE [PartDesign::Pad] Pad012
  BaseFeature = -> Pad008
  Direction = (0,0,1)
  Length = 5
  Length2 = 10
  Profile = -> Sketch018
  ReferenceAxis = -> Sketch018 [N_Axis]
  Reversed = true
  SideType = 0
  Suppressed = false
  Type = 0
  Type2 = 0
FEATURE [PartDesign::Body] Body002  label="Lid"
  AllowCompound = false
  Group = -> [Binder001,Sketch013,Pad008,Sketch018,Pad012]
  Origin = -> Origin002
  Placement = pos=(0,0,42.5) rot=(0,0,1;0rad)
  Tip = -> Pad012
FEATURE [Sketcher::SketchObject] Sketch019  label="SealOuterwallSketch"
  ArcFitTolerance = 1e-06
  AttachmentSupport = -> [XY_Plane001]
  ExternalGeometry = -> [Sketch008]
  ExternalTypes = [0]
  FullyConstrained = true
  MakeInternals = false
  MapMode = 5
  _ExternalGeoVersion = 0
  expr: Constraints[37] = <<sheet>>.LidWallAroundSides
  expr: Constraints[38] = .Constraints.Margin
  sketch-geometry (18):
    g0: LineSegment StartX=-50.2 StartY=41 StartZ=0 EndX=-50.2 EndY=-41 EndZ=0
    g1: LineSegment StartX=-47.7 StartY=-43.5 StartZ=0 EndX=47.5 EndY=-43.5 EndZ=0
    g2: LineSegment StartX=50 StartY=-41 StartZ=0 EndX=50 EndY=41 EndZ=0
    g3: LineSegment StartX=47.5 StartY=43.5 StartZ=0 EndX=-47.7 EndY=43.5 EndZ=0
    g4: ArcOfCircle CenterX=-47.7 CenterY=41 CenterZ=0 NormalX=0 NormalY=0 NormalZ=1 AngleXU=0 Radius=2.5 StartAngle=1.5708 EndAngle=3.14159
    g5: ArcOfCircle CenterX=-47.7 CenterY=-41 CenterZ=0 NormalX=0 NormalY=0 NormalZ=1 AngleXU=0 Radius=2.5 StartAngle=3.14159 EndAngle=4.71239
    g6: ArcOfCircle CenterX=47.5 CenterY=-41 CenterZ=0 NormalX=0 NormalY=0 NormalZ=1 AngleXU=0 Radius=2.5 StartAngle=4.71239 EndAngle=6.28319
    g7: ArcOfCircle CenterX=47.5 CenterY=41 CenterZ=0 NormalX=0 NormalY=0 NormalZ=1 AngleXU=0 Radius=2.5 StartAngle=-9e-16 EndAngle=1.5708
    g8: LineSegment StartX=-49.1 StartY=41 StartZ=0 EndX=-49.1 EndY=-41 EndZ=0
    g9: LineSegment StartX=-47.7 StartY=-42.4 StartZ=0 EndX=47.5 EndY=-42.4 EndZ=0
    g10: LineSegment StartX=48.9 StartY=-41 StartZ=0 EndX=48.9 EndY=41 EndZ=0
    g11: LineSegment StartX=47.5 StartY=42.4 StartZ=0 EndX=-47.7 EndY=42.4 EndZ=0
    g12: ArcOfCircle CenterX=-47.7 CenterY=41 CenterZ=0 NormalX=0 NormalY=0 NormalZ=1 AngleXU=0 Radius=1.4 StartAngle=1.5708 EndAngle=3.14159
    g13: ArcOfCircle CenterX=-47.7 CenterY=-41 CenterZ=0 NormalX=0 NormalY=0 NormalZ=1 AngleXU=0 Radius=1.4 StartAngle=3.14159 EndAngle=4.71239
    g14: ArcOfCircle CenterX=47.5 CenterY=-41 CenterZ=0 NormalX=0 NormalY=0 NormalZ=1 AngleXU=0 Radius=1.4 StartAngle=4.71239 EndAngle=6.28319
    g15: ArcOfCircle CenterX=47.5 CenterY=41 CenterZ=0 NormalX=0 NormalY=0 NormalZ=1 AngleXU=0 Radius=1.4 StartAngle=2e-16 EndAngle=1.5708
    g16: GeomPoint [constr] X=-50.2 Y=43.5 Z=0
    g17: GeomPoint [constr] X=50 Y=-43.5 Z=0
  constraints (40):
    c: Tangent(g0,g4) = -1.5708
    c: Tangent(g0,g5) = -1.5708
    c: Tangent(g1,g5) = -1.5708
    c: Tangent(g1,g6) = -1.5708
    c: Tangent(g2,g6) = -1.5708
    c: Tangent(g2,g7) = -1.5708
    c: Tangent(g3,g7) = -1.5708
    c: Tangent(g3,g4) = -1.5708
    c: Vertical(g0)
    c: Vertical(g2)
    c: Horizontal(g1)
    c: Horizontal(g3)
    c: Equal(g4,g5)
    c: Equal(g5,g6)
    c: Equal(g6,g7)
    c: Tangent(g8,g12) = -1.5708
    c: Tangent(g8,g13) = -1.5708
    c: Tangent(g9,g13) = -1.5708
    c: Tangent(g9,g14) = -1.5708
    c: Tangent(g10,g14) = -1.5708
    c: Tangent(g10,g15) = -1.5708
    c: Tangent(g11,g15) = -1.5708
    c: Tangent(g11,g12) = -1.5708
    c: Coincident(g4,g12)
    c: Coincident(g5,g13)
    c: Coincident(g6,g14)
    c: Coincident(g7,g15)
    c: Vertical(g8)
    c: Vertical(g10)
    c: Horizontal(g9)
    c: PointOnObject(g16,g0)
    c: PointOnObject(g16,g3)
    c: PointOnObject(g17,g1)
    c: PointOnObject(g17,g2)
    c: DistanceX(g10,g-4) = 0.1  'Margin'
    c: Horizontal(g10,g-4)
    c: Vertical(g3,g-3)
    c: DistanceY(g-3,g3) = 1
    c: Distance(g8,g-5) = 0.1
    c: Horizontal(g8,g-5)
FEATURE [PartDesign::Pad] Pad013  label="SealOuterwall"
  BaseFeature = -> Pad007
  Direction = (0,0,1)
  Length = 4
  Length2 = 10
  Profile = -> Sketch019
  ReferenceAxis = -> Sketch019 [N_Axis]
  SideType = 0
  Suppressed = false
  Type = 0
  Type2 = 0
FEATURE [PartDesign::Body] Body001  label="Seal"
  AllowCompound = false
  Group = -> [Sketch008,Pad006,Sketch009,DatumPlane001,Sketch010,AdditiveLoft,Sketch011,Binder,Pocket002,Sketch012,Pad007,Sketch019,Pad013]
  Origin = -> Origin001
  Placement = pos=(-3.2e-15,0,36.6) rot=(0,1,0;3.14159rad)
  Tip = -> Pad013
FEATURE [PartDesign::Pad] Pad014  label="BoxBatteryClip2"
  BaseFeature = -> Pocket001
  Direction = (1,0,0)
  Length = 1
  Length2 = 10
  Profile = -> Sketch006
  ReferenceAxis = -> Sketch006 [N_Axis]
  SideType = 0
  Suppressed = false
  Type = 0
  Type2 = 0
FEATURE [PartDesign::Body] Body  label="Box"
  AllowCompound = false
  Group = -> [Sketch,Pad,Sketch001,Pad001,Sketch002,Pad002,Sketch003,Pad003,Sketch004,Pocket,Sketch005,Pad004,Sketch006,DatumPlane,Sketch007,Pocket001,Pad014]
  Origin = -> Origin
  Tip = -> Pad014
FEATURE [Sketcher::SketchObject] Sketch020
  ArcFitTolerance = 1e-06
  AttachmentSupport = -> [XY_Plane004]
  ExternalTypes = [0]
  FullyConstrained = true
  MakeInternals = false
  MapMode = 5
  _ExternalGeoVersion = 0
  expr: Constraints[10] = <<sheet>>.PanelLength
  expr: Constraints[11] = <<sheet>>.PanelWidth
  sketch-geometry (5):
    g0: LineSegment StartX=47.5 StartY=-37.5 StartZ=0 EndX=47.5 EndY=37.5 EndZ=0
    g1: LineSegment StartX=47.5 StartY=37.5 StartZ=0 EndX=-47.5 EndY=37.5 EndZ=0
    g2: LineSegment StartX=-47.5 StartY=37.5 StartZ=0 EndX=-47.5 EndY=-37.5 EndZ=0
    g3: LineSegment StartX=-47.5 StartY=-37.5 StartZ=0 EndX=47.5 EndY=-37.5 EndZ=0
    g4: GeomPoint [constr] X=0 Y=0 Z=0
  constraints (12):
    c: Coincident(g0,g1)
    c: Coincident(g1,g2)
    c: Coincident(g2,g3)
    c: Coincident(g3,g0)
    c: Vertical(g0)
    c: Vertical(g2)
    c: Horizontal(g1)
    c: Horizontal(g3)
    c: Symmetric(g2,g0,g4)
    c: Coincident(g4,g-1)
    c: DistanceX(g1,g1) = 95
    c: DistanceY(g0,g0) = 75
FEATURE [PartDesign::Pad] Pad015
  Direction = (0,0,1)
  Length = 2
  Length2 = 10
  Profile = -> Sketch020
  ReferenceAxis = -> Sketch020 [N_Axis]
  SideType = 0
  Suppressed = false
  Type = 0
  Type2 = 0
FEATURE [PartDesign::Body] Body004  label="SolarPanel"
  AllowCompound = false
  Group = -> [Sketch020,Pad015]
  Origin = -> Origin004
  Placement = pos=(0,-4.7,-13.3) rot=(0,0,1;0rad)
  Tip = -> Pad015
FEATURE [App::Point] Origin005  label="Origin"
  Role = Origin
FEATURE [App::Point] Origin006  label="Origin"
  Role = Origin
FEATURE [App::Point] Origin007  label="Origin"
  Role = Origin
FEATURE [App::Point] Origin008  label="Origin"
  Role = Origin
FEATURE [App::Point] Origin009  label="Origin"
  Role = Origin
